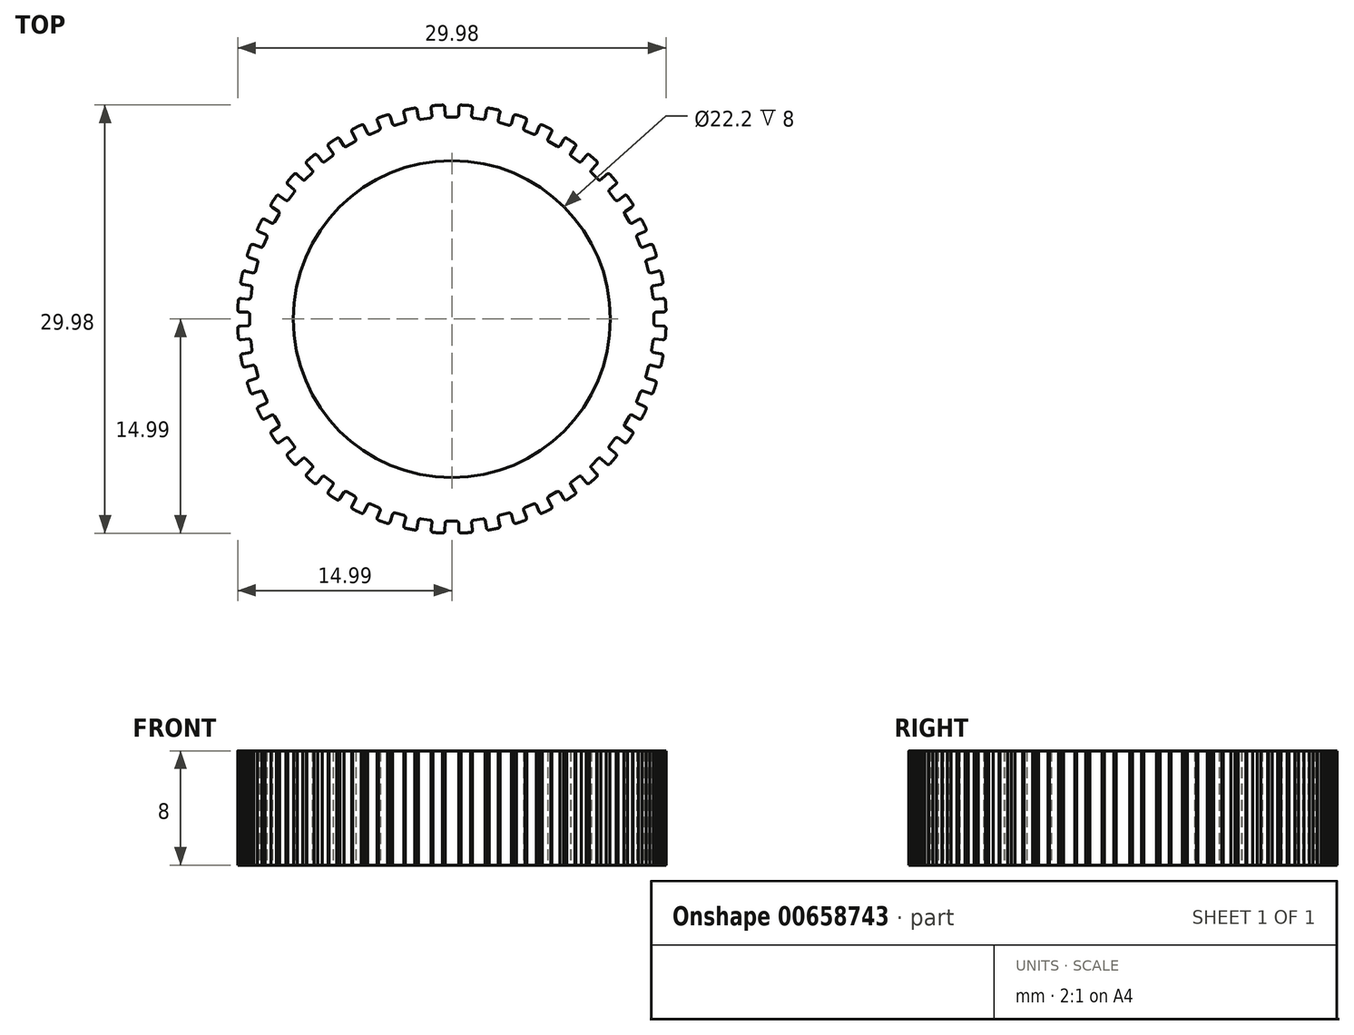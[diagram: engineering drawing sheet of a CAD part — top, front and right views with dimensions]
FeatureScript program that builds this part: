
annotation { "Feature Type Name" : "Feature", "Feature Type Description" : "" }
export const myFeature = defineFeature(function(context is Context, id is Id, definition is map)
    precondition{}
    {
        {
            assignVariable(context, id + "F0", {"name" : "h", "anyValue" : 8});
        }
        {
            var Q0;
            Q0=qCreatedBy(makeId("Top.planeOp"),FACE);
            var sketch = newSketch(context, id + "F1", { "sketchPlane" : qUnion([Q0])});
            skCircle(sketch, "E0", {"center": v(0, 0) * mm, "radius": 15 * mm});
            skCircle(sketch, "E1", {"center": v(0, 0) * mm, "radius": 11.1 * mm});
            skSolve(sketch);
        }
        {
            var Q0;
            Q0=qCreatedBy(makeId("Top.planeOp"),FACE);
            var sketch = newSketch(context, id + "F2", { "sketchPlane" : qUnion([Q0])});
            skCircle(sketch, "E2.0", {"center": v(0, 0) * mm, "radius": 15 * mm});
            skLineSegment(sketch, "E3.top", {"start": v(-0.65, 15.23) * mm, "end": v(0.65, 15.23) * mm});
            skLineSegment(sketch, "E3.left", {"start": v(-0.65, 14.99) * mm, "end": v(-0.65, 15.23) * mm});
            skLineSegment(sketch, "E4", {"start": v(0, 0) * mm, "end": v(-0.5, 15) * mm, "construction": true});
            skArc(sketch, "E5", {"start": v(-0.5, 14.8) * mm, "mid": v(-0.53, 14.93) * mm, "end": v(-0.65, 14.99) * mm});
            skPoint(sketch, "E6", {"position": v(0, 14.15) * mm});
            skLineSegment(sketch, "E7", {"start": v(0, 14.15) * mm, "end": v(-0.32, 14.15) * mm});
            skArc(sketch, "E8", {"start": v(-0.48, 14.27) * mm, "mid": v(-0.42, 14.19) * mm, "end": v(-0.32, 14.15) * mm});
            skArc(sketch, "E9.MirrorCS", {"start": v(0.5, 14.8) * mm, "mid": v(0.53, 14.93) * mm, "end": v(0.65, 14.99) * mm});
            skLineSegment(sketch, "E10", {"start": v(-0.5, 14.8) * mm, "end": v(-0.48, 14.27) * mm});
            skArc(sketch, "E11.MirrorCS", {"start": v(0.48, 14.27) * mm, "mid": v(0.42, 14.19) * mm, "end": v(0.32, 14.15) * mm});
            skLineSegment(sketch, "E12.MirrorCS", {"start": v(0, 0) * mm, "end": v(0.5, 15) * mm, "construction": true});
            skLineSegment(sketch, "E13.MirrorCS", {"start": v(0, 14.15) * mm, "end": v(0.32, 14.15) * mm});
            skLineSegment(sketch, "E14.MirrorCS", {"start": v(0.5, 14.8) * mm, "end": v(0.48, 14.27) * mm});
            skLineSegment(sketch, "E15.MirrorCS", {"start": v(0.65, 14.99) * mm, "end": v(0.65, 15.23) * mm});
            skSolve(sketch);
        }
        {
            var Q0;
            Q0=qCreatedBy(makeId("Top.planeOp"),FACE);
            var sketch = newSketch(context, id + "F3", { "sketchPlane" : qUnion([Q0])});
            skLineSegment(sketch, "E16.0", {"start": v(-0.65, 14.99) * mm, "end": v(-0.65, 15.23) * mm});
            skLineSegment(sketch, "E16.1", {"start": v(0, 14.15) * mm, "end": v(-0.32, 14.15) * mm});
            skLineSegment(sketch, "E16.2", {"start": v(-0.65, 15.23) * mm, "end": v(0.65, 15.23) * mm});
            skLineSegment(sketch, "E16.3", {"start": v(0.65, 14.99) * mm, "end": v(0.65, 15.23) * mm});
            skLineSegment(sketch, "E16.4", {"start": v(0.5, 14.8) * mm, "end": v(0.48, 14.27) * mm});
            skArc(sketch, "E16.5", {"start": v(-0.5, 14.8) * mm, "mid": v(-0.53, 14.93) * mm, "end": v(-0.65, 14.99) * mm});
            skArc(sketch, "E16.6", {"start": v(0.5, 14.8) * mm, "mid": v(0.53, 14.93) * mm, "end": v(0.65, 14.99) * mm});
            skArc(sketch, "E16.7", {"start": v(-0.48, 14.27) * mm, "mid": v(-0.42, 14.19) * mm, "end": v(-0.32, 14.15) * mm});
            skLineSegment(sketch, "E16.8", {"start": v(-0.5, 14.8) * mm, "end": v(-0.48, 14.27) * mm});
            skLineSegment(sketch, "E16.9", {"start": v(0, 14.15) * mm, "end": v(0.32, 14.15) * mm});
            skArc(sketch, "E16.10", {"start": v(0.48, 14.27) * mm, "mid": v(0.42, 14.19) * mm, "end": v(0.32, 14.15) * mm});
            skLineSegment(sketch, "E17.1.0", {"start": v(-1.31, 14.94) * mm, "end": v(-1.34, 15.19) * mm});
            skLineSegment(sketch, "E17.1.1", {"start": v(-1.44, 14.74) * mm, "end": v(-1.4, 14.21) * mm});
            skArc(sketch, "E17.1.2", {"start": v(-2.42, 14.6) * mm, "mid": v(-2.47, 14.73) * mm, "end": v(-2.6, 14.77) * mm});
            skArc(sketch, "E17.1.3", {"start": v(-1.44, 14.74) * mm, "mid": v(-1.42, 14.87) * mm, "end": v(-1.31, 14.94) * mm});
            skArc(sketch, "E17.1.4", {"start": v(-2.34, 14.1) * mm, "mid": v(-2.27, 14) * mm, "end": v(-2.16, 13.99) * mm});
            skLineSegment(sketch, "E17.1.5", {"start": v(-2.42, 14.6) * mm, "end": v(-2.34, 14.1) * mm});
            skLineSegment(sketch, "E17.1.6", {"start": v(-1.85, 14.03) * mm, "end": v(-1.53, 14.07) * mm});
            skArc(sketch, "E17.1.7", {"start": v(-1.4, 14.21) * mm, "mid": v(-1.44, 14.12) * mm, "end": v(-1.53, 14.07) * mm});
            skLineSegment(sketch, "E17.1.8", {"start": v(-2.63, 15.02) * mm, "end": v(-1.34, 15.19) * mm});
            skLineSegment(sketch, "E17.1.9", {"start": v(-1.85, 14.03) * mm, "end": v(-2.16, 13.99) * mm});
            skLineSegment(sketch, "E17.1.10", {"start": v(-2.6, 14.77) * mm, "end": v(-2.63, 15.02) * mm});
            skLineSegment(sketch, "E17.2.0", {"start": v(-3.25, 14.64) * mm, "end": v(-3.31, 14.88) * mm});
            skLineSegment(sketch, "E17.2.1", {"start": v(-3.35, 14.42) * mm, "end": v(-3.23, 13.91) * mm});
            skArc(sketch, "E17.2.2", {"start": v(-4.3, 14.17) * mm, "mid": v(-4.37, 14.28) * mm, "end": v(-4.5, 14.3) * mm});
            skArc(sketch, "E17.2.3", {"start": v(-3.35, 14.42) * mm, "mid": v(-3.35, 14.56) * mm, "end": v(-3.25, 14.64) * mm});
            skArc(sketch, "E17.2.4", {"start": v(-4.15, 13.67) * mm, "mid": v(-4.08, 13.6) * mm, "end": v(-3.97, 13.59) * mm});
            skLineSegment(sketch, "E17.2.5", {"start": v(-4.3, 14.17) * mm, "end": v(-4.15, 13.67) * mm});
            skLineSegment(sketch, "E17.2.6", {"start": v(-3.66, 13.67) * mm, "end": v(-3.35, 13.75) * mm});
            skArc(sketch, "E17.2.7", {"start": v(-3.23, 13.91) * mm, "mid": v(-3.27, 13.81) * mm, "end": v(-3.35, 13.75) * mm});
            skLineSegment(sketch, "E17.2.8", {"start": v(-4.57, 14.55) * mm, "end": v(-3.31, 14.88) * mm});
            skLineSegment(sketch, "E17.2.9", {"start": v(-3.66, 13.67) * mm, "end": v(-3.97, 13.59) * mm});
            skLineSegment(sketch, "E17.2.10", {"start": v(-4.5, 14.3) * mm, "end": v(-4.57, 14.55) * mm});
            skLineSegment(sketch, "E17.3.0", {"start": v(-5.13, 14.1) * mm, "end": v(-5.23, 14.32) * mm});
            skLineSegment(sketch, "E17.3.1", {"start": v(-5.2, 13.86) * mm, "end": v(-5.02, 13.37) * mm});
            skArc(sketch, "E17.3.2", {"start": v(-6.12, 13.48) * mm, "mid": v(-6.2, 13.59) * mm, "end": v(-6.34, 13.6) * mm});
            skArc(sketch, "E17.3.3", {"start": v(-5.2, 13.86) * mm, "mid": v(-5.22, 14) * mm, "end": v(-5.13, 14.1) * mm});
            skArc(sketch, "E17.3.4", {"start": v(-5.9, 13) * mm, "mid": v(-5.82, 12.94) * mm, "end": v(-5.71, 12.95) * mm});
            skLineSegment(sketch, "E17.3.5", {"start": v(-6.12, 13.48) * mm, "end": v(-5.9, 13) * mm});
            skLineSegment(sketch, "E17.3.6", {"start": v(-5.41, 13.07) * mm, "end": v(-5.12, 13.2) * mm});
            skArc(sketch, "E17.3.7", {"start": v(-5.02, 13.37) * mm, "mid": v(-5.04, 13.27) * mm, "end": v(-5.12, 13.2) * mm});
            skLineSegment(sketch, "E17.3.8", {"start": v(-6.43, 13.82) * mm, "end": v(-5.23, 14.32) * mm});
            skLineSegment(sketch, "E17.3.9", {"start": v(-5.41, 13.07) * mm, "end": v(-5.71, 12.95) * mm});
            skLineSegment(sketch, "E17.3.10", {"start": v(-6.34, 13.6) * mm, "end": v(-6.43, 13.82) * mm});
            skLineSegment(sketch, "E17.4.0", {"start": v(-6.93, 13.3) * mm, "end": v(-7.05, 13.52) * mm});
            skLineSegment(sketch, "E17.4.1", {"start": v(-6.97, 13.06) * mm, "end": v(-6.73, 12.6) * mm});
            skArc(sketch, "E17.4.2", {"start": v(-7.83, 12.57) * mm, "mid": v(-7.92, 12.66) * mm, "end": v(-8.06, 12.65) * mm});
            skArc(sketch, "E17.4.3", {"start": v(-6.97, 13.06) * mm, "mid": v(-7, 13.2) * mm, "end": v(-6.93, 13.3) * mm});
            skArc(sketch, "E17.4.4", {"start": v(-7.55, 12.12) * mm, "mid": v(-7.46, 12.07) * mm, "end": v(-7.35, 12.1) * mm});
            skLineSegment(sketch, "E17.4.5", {"start": v(-7.83, 12.57) * mm, "end": v(-7.55, 12.12) * mm});
            skLineSegment(sketch, "E17.4.6", {"start": v(-7.08, 12.25) * mm, "end": v(-6.8, 12.41) * mm});
            skArc(sketch, "E17.4.7", {"start": v(-6.73, 12.6) * mm, "mid": v(-6.73, 12.5) * mm, "end": v(-6.8, 12.41) * mm});
            skLineSegment(sketch, "E17.4.8", {"start": v(-8.18, 12.87) * mm, "end": v(-7.05, 13.52) * mm});
            skLineSegment(sketch, "E17.4.9", {"start": v(-7.08, 12.25) * mm, "end": v(-7.35, 12.1) * mm});
            skLineSegment(sketch, "E17.4.10", {"start": v(-8.06, 12.65) * mm, "end": v(-8.18, 12.87) * mm});
            skLineSegment(sketch, "E17.5.0", {"start": v(-8.6, 12.28) * mm, "end": v(-8.76, 12.48) * mm});
            skLineSegment(sketch, "E17.5.1", {"start": v(-8.62, 12.04) * mm, "end": v(-8.31, 11.61) * mm});
            skArc(sketch, "E17.5.2", {"start": v(-9.4, 11.44) * mm, "mid": v(-9.5, 11.52) * mm, "end": v(-9.64, 11.5) * mm});
            skArc(sketch, "E17.5.3", {"start": v(-8.62, 12.04) * mm, "mid": v(-8.67, 12.17) * mm, "end": v(-8.6, 12.28) * mm});
            skArc(sketch, "E17.5.4", {"start": v(-9.07, 11.04) * mm, "mid": v(-8.97, 11) * mm, "end": v(-8.87, 11.03) * mm});
            skLineSegment(sketch, "E17.5.5", {"start": v(-9.4, 11.44) * mm, "end": v(-9.07, 11.04) * mm});
            skLineSegment(sketch, "E17.5.6", {"start": v(-8.61, 11.23) * mm, "end": v(-8.36, 11.42) * mm});
            skArc(sketch, "E17.5.7", {"start": v(-8.31, 11.61) * mm, "mid": v(-8.3, 11.5) * mm, "end": v(-8.36, 11.42) * mm});
            skLineSegment(sketch, "E17.5.8", {"start": v(-9.79, 11.69) * mm, "end": v(-8.76, 12.48) * mm});
            skLineSegment(sketch, "E17.5.9", {"start": v(-8.61, 11.23) * mm, "end": v(-8.87, 11.03) * mm});
            skLineSegment(sketch, "E17.5.10", {"start": v(-9.64, 11.5) * mm, "end": v(-9.79, 11.69) * mm});
            skLineSegment(sketch, "E17.6.0", {"start": v(-10.14, 11.06) * mm, "end": v(-10.31, 11.23) * mm});
            skLineSegment(sketch, "E17.6.1", {"start": v(-10.12, 10.81) * mm, "end": v(-9.76, 10.43) * mm});
            skArc(sketch, "E17.6.2", {"start": v(-10.81, 10.12) * mm, "mid": v(-10.93, 10.18) * mm, "end": v(-11.06, 10.14) * mm});
            skArc(sketch, "E17.6.3", {"start": v(-10.12, 10.81) * mm, "mid": v(-10.18, 10.93) * mm, "end": v(-10.14, 11.06) * mm});
            skArc(sketch, "E17.6.4", {"start": v(-10.43, 9.76) * mm, "mid": v(-10.33, 9.73) * mm, "end": v(-10.23, 9.78) * mm});
            skLineSegment(sketch, "E17.6.5", {"start": v(-10.81, 10.12) * mm, "end": v(-10.43, 9.76) * mm});
            skLineSegment(sketch, "E17.6.6", {"start": v(-10, 10) * mm, "end": v(-9.78, 10.23) * mm});
            skArc(sketch, "E17.6.7", {"start": v(-9.76, 10.43) * mm, "mid": v(-9.73, 10.33) * mm, "end": v(-9.78, 10.23) * mm});
            skLineSegment(sketch, "E17.6.8", {"start": v(-11.23, 10.31) * mm, "end": v(-10.31, 11.23) * mm});
            skLineSegment(sketch, "E17.6.9", {"start": v(-10, 10) * mm, "end": v(-10.23, 9.78) * mm});
            skLineSegment(sketch, "E17.6.10", {"start": v(-11.06, 10.14) * mm, "end": v(-11.23, 10.31) * mm});
            skLineSegment(sketch, "E17.7.0", {"start": v(-11.5, 9.64) * mm, "end": v(-11.69, 9.79) * mm});
            skLineSegment(sketch, "E17.7.1", {"start": v(-11.44, 9.4) * mm, "end": v(-11.04, 9.07) * mm});
            skArc(sketch, "E17.7.2", {"start": v(-12.04, 8.62) * mm, "mid": v(-12.17, 8.67) * mm, "end": v(-12.28, 8.6) * mm});
            skArc(sketch, "E17.7.3", {"start": v(-11.44, 9.4) * mm, "mid": v(-11.52, 9.5) * mm, "end": v(-11.5, 9.64) * mm});
            skArc(sketch, "E17.7.4", {"start": v(-11.61, 8.31) * mm, "mid": v(-11.5, 8.3) * mm, "end": v(-11.42, 8.36) * mm});
            skLineSegment(sketch, "E17.7.5", {"start": v(-12.04, 8.62) * mm, "end": v(-11.61, 8.31) * mm});
            skLineSegment(sketch, "E17.7.6", {"start": v(-11.23, 8.61) * mm, "end": v(-11.03, 8.87) * mm});
            skArc(sketch, "E17.7.7", {"start": v(-11.04, 9.07) * mm, "mid": v(-11, 8.97) * mm, "end": v(-11.03, 8.87) * mm});
            skLineSegment(sketch, "E17.7.8", {"start": v(-12.48, 8.76) * mm, "end": v(-11.69, 9.79) * mm});
            skLineSegment(sketch, "E17.7.9", {"start": v(-11.23, 8.61) * mm, "end": v(-11.42, 8.36) * mm});
            skLineSegment(sketch, "E17.7.10", {"start": v(-12.28, 8.6) * mm, "end": v(-12.48, 8.76) * mm});
            skLineSegment(sketch, "E17.8.0", {"start": v(-12.65, 8.06) * mm, "end": v(-12.87, 8.18) * mm});
            skLineSegment(sketch, "E17.8.1", {"start": v(-12.57, 7.83) * mm, "end": v(-12.12, 7.55) * mm});
            skArc(sketch, "E17.8.2", {"start": v(-13.06, 6.97) * mm, "mid": v(-13.2, 7) * mm, "end": v(-13.3, 6.93) * mm});
            skArc(sketch, "E17.8.3", {"start": v(-12.57, 7.83) * mm, "mid": v(-12.66, 7.92) * mm, "end": v(-12.65, 8.06) * mm});
            skArc(sketch, "E17.8.4", {"start": v(-12.6, 6.73) * mm, "mid": v(-12.5, 6.73) * mm, "end": v(-12.41, 6.8) * mm});
            skLineSegment(sketch, "E17.8.5", {"start": v(-13.06, 6.97) * mm, "end": v(-12.6, 6.73) * mm});
            skLineSegment(sketch, "E17.8.6", {"start": v(-12.25, 7.08) * mm, "end": v(-12.1, 7.35) * mm});
            skArc(sketch, "E17.8.7", {"start": v(-12.12, 7.55) * mm, "mid": v(-12.07, 7.46) * mm, "end": v(-12.1, 7.35) * mm});
            skLineSegment(sketch, "E17.8.8", {"start": v(-13.52, 7.05) * mm, "end": v(-12.87, 8.18) * mm});
            skLineSegment(sketch, "E17.8.9", {"start": v(-12.25, 7.08) * mm, "end": v(-12.41, 6.8) * mm});
            skLineSegment(sketch, "E17.8.10", {"start": v(-13.3, 6.93) * mm, "end": v(-13.52, 7.05) * mm});
            skLineSegment(sketch, "E17.9.0", {"start": v(-13.6, 6.34) * mm, "end": v(-13.82, 6.43) * mm});
            skLineSegment(sketch, "E17.9.1", {"start": v(-13.48, 6.12) * mm, "end": v(-13, 5.9) * mm});
            skArc(sketch, "E17.9.2", {"start": v(-13.86, 5.2) * mm, "mid": v(-14, 5.22) * mm, "end": v(-14.1, 5.13) * mm});
            skArc(sketch, "E17.9.3", {"start": v(-13.48, 6.12) * mm, "mid": v(-13.59, 6.2) * mm, "end": v(-13.6, 6.34) * mm});
            skArc(sketch, "E17.9.4", {"start": v(-13.37, 5.02) * mm, "mid": v(-13.27, 5.04) * mm, "end": v(-13.2, 5.12) * mm});
            skLineSegment(sketch, "E17.9.5", {"start": v(-13.86, 5.2) * mm, "end": v(-13.37, 5.02) * mm});
            skLineSegment(sketch, "E17.9.6", {"start": v(-13.07, 5.41) * mm, "end": v(-12.95, 5.71) * mm});
            skArc(sketch, "E17.9.7", {"start": v(-13, 5.9) * mm, "mid": v(-12.94, 5.82) * mm, "end": v(-12.95, 5.71) * mm});
            skLineSegment(sketch, "E17.9.8", {"start": v(-14.32, 5.23) * mm, "end": v(-13.82, 6.43) * mm});
            skLineSegment(sketch, "E17.9.9", {"start": v(-13.07, 5.41) * mm, "end": v(-13.2, 5.12) * mm});
            skLineSegment(sketch, "E17.9.10", {"start": v(-14.1, 5.13) * mm, "end": v(-14.32, 5.23) * mm});
            skLineSegment(sketch, "E17.10.0", {"start": v(-14.3, 4.5) * mm, "end": v(-14.55, 4.57) * mm});
            skLineSegment(sketch, "E17.10.1", {"start": v(-14.17, 4.3) * mm, "end": v(-13.67, 4.15) * mm});
            skArc(sketch, "E17.10.2", {"start": v(-14.42, 3.35) * mm, "mid": v(-14.56, 3.35) * mm, "end": v(-14.64, 3.25) * mm});
            skArc(sketch, "E17.10.3", {"start": v(-14.17, 4.3) * mm, "mid": v(-14.28, 4.37) * mm, "end": v(-14.3, 4.5) * mm});
            skArc(sketch, "E17.10.4", {"start": v(-13.91, 3.23) * mm, "mid": v(-13.81, 3.27) * mm, "end": v(-13.75, 3.35) * mm});
            skLineSegment(sketch, "E17.10.5", {"start": v(-14.42, 3.35) * mm, "end": v(-13.91, 3.23) * mm});
            skLineSegment(sketch, "E17.10.6", {"start": v(-13.67, 3.66) * mm, "end": v(-13.59, 3.97) * mm});
            skArc(sketch, "E17.10.7", {"start": v(-13.67, 4.15) * mm, "mid": v(-13.6, 4.08) * mm, "end": v(-13.59, 3.97) * mm});
            skLineSegment(sketch, "E17.10.8", {"start": v(-14.88, 3.31) * mm, "end": v(-14.55, 4.57) * mm});
            skLineSegment(sketch, "E17.10.9", {"start": v(-13.67, 3.66) * mm, "end": v(-13.75, 3.35) * mm});
            skLineSegment(sketch, "E17.10.10", {"start": v(-14.64, 3.25) * mm, "end": v(-14.88, 3.31) * mm});
            skLineSegment(sketch, "E17.11.0", {"start": v(-14.77, 2.6) * mm, "end": v(-15.02, 2.63) * mm});
            skLineSegment(sketch, "E17.11.1", {"start": v(-14.6, 2.42) * mm, "end": v(-14.1, 2.34) * mm});
            skArc(sketch, "E17.11.2", {"start": v(-14.74, 1.44) * mm, "mid": v(-14.87, 1.42) * mm, "end": v(-14.94, 1.31) * mm});
            skArc(sketch, "E17.11.3", {"start": v(-14.6, 2.42) * mm, "mid": v(-14.73, 2.47) * mm, "end": v(-14.77, 2.6) * mm});
            skArc(sketch, "E17.11.4", {"start": v(-14.21, 1.4) * mm, "mid": v(-14.12, 1.44) * mm, "end": v(-14.07, 1.53) * mm});
            skLineSegment(sketch, "E17.11.5", {"start": v(-14.74, 1.44) * mm, "end": v(-14.21, 1.4) * mm});
            skLineSegment(sketch, "E17.11.6", {"start": v(-14.03, 1.85) * mm, "end": v(-13.99, 2.16) * mm});
            skArc(sketch, "E17.11.7", {"start": v(-14.1, 2.34) * mm, "mid": v(-14, 2.27) * mm, "end": v(-13.99, 2.16) * mm});
            skLineSegment(sketch, "E17.11.8", {"start": v(-15.19, 1.34) * mm, "end": v(-15.02, 2.63) * mm});
            skLineSegment(sketch, "E17.11.9", {"start": v(-14.03, 1.85) * mm, "end": v(-14.07, 1.53) * mm});
            skLineSegment(sketch, "E17.11.10", {"start": v(-14.94, 1.31) * mm, "end": v(-15.19, 1.34) * mm});
            skLineSegment(sketch, "E17.12.0", {"start": v(-14.99, 0.65) * mm, "end": v(-15.23, 0.65) * mm});
            skLineSegment(sketch, "E17.12.1", {"start": v(-14.8, 0.5) * mm, "end": v(-14.27, 0.48) * mm});
            skArc(sketch, "E17.12.2", {"start": v(-14.8, -0.5) * mm, "mid": v(-14.93, -0.53) * mm, "end": v(-14.99, -0.65) * mm});
            skArc(sketch, "E17.12.3", {"start": v(-14.8, 0.5) * mm, "mid": v(-14.93, 0.53) * mm, "end": v(-14.99, 0.65) * mm});
            skArc(sketch, "E17.12.4", {"start": v(-14.27, -0.48) * mm, "mid": v(-14.19, -0.42) * mm, "end": v(-14.15, -0.32) * mm});
            skLineSegment(sketch, "E17.12.5", {"start": v(-14.8, -0.5) * mm, "end": v(-14.27, -0.48) * mm});
            skLineSegment(sketch, "E17.12.6", {"start": v(-14.15, 0) * mm, "end": v(-14.15, 0.32) * mm});
            skArc(sketch, "E17.12.7", {"start": v(-14.27, 0.48) * mm, "mid": v(-14.19, 0.42) * mm, "end": v(-14.15, 0.32) * mm});
            skLineSegment(sketch, "E17.12.8", {"start": v(-15.23, -0.65) * mm, "end": v(-15.23, 0.65) * mm});
            skLineSegment(sketch, "E17.12.9", {"start": v(-14.15, 0) * mm, "end": v(-14.15, -0.32) * mm});
            skLineSegment(sketch, "E17.12.10", {"start": v(-14.99, -0.65) * mm, "end": v(-15.23, -0.65) * mm});
            skLineSegment(sketch, "E17.13.0", {"start": v(-14.94, -1.31) * mm, "end": v(-15.19, -1.34) * mm});
            skLineSegment(sketch, "E17.13.1", {"start": v(-14.74, -1.44) * mm, "end": v(-14.21, -1.4) * mm});
            skArc(sketch, "E17.13.2", {"start": v(-14.6, -2.42) * mm, "mid": v(-14.73, -2.47) * mm, "end": v(-14.77, -2.6) * mm});
            skArc(sketch, "E17.13.3", {"start": v(-14.74, -1.44) * mm, "mid": v(-14.87, -1.42) * mm, "end": v(-14.94, -1.31) * mm});
            skArc(sketch, "E17.13.4", {"start": v(-14.1, -2.34) * mm, "mid": v(-14, -2.27) * mm, "end": v(-13.99, -2.16) * mm});
            skLineSegment(sketch, "E17.13.5", {"start": v(-14.6, -2.42) * mm, "end": v(-14.1, -2.34) * mm});
            skLineSegment(sketch, "E17.13.6", {"start": v(-14.03, -1.85) * mm, "end": v(-14.07, -1.53) * mm});
            skArc(sketch, "E17.13.7", {"start": v(-14.21, -1.4) * mm, "mid": v(-14.12, -1.44) * mm, "end": v(-14.07, -1.53) * mm});
            skLineSegment(sketch, "E17.13.8", {"start": v(-15.02, -2.63) * mm, "end": v(-15.19, -1.34) * mm});
            skLineSegment(sketch, "E17.13.9", {"start": v(-14.03, -1.85) * mm, "end": v(-13.99, -2.16) * mm});
            skLineSegment(sketch, "E17.13.10", {"start": v(-14.77, -2.6) * mm, "end": v(-15.02, -2.63) * mm});
            skLineSegment(sketch, "E17.14.0", {"start": v(-14.64, -3.25) * mm, "end": v(-14.88, -3.31) * mm});
            skLineSegment(sketch, "E17.14.1", {"start": v(-14.42, -3.35) * mm, "end": v(-13.91, -3.23) * mm});
            skArc(sketch, "E17.14.2", {"start": v(-14.17, -4.3) * mm, "mid": v(-14.28, -4.37) * mm, "end": v(-14.3, -4.5) * mm});
            skArc(sketch, "E17.14.3", {"start": v(-14.42, -3.35) * mm, "mid": v(-14.56, -3.35) * mm, "end": v(-14.64, -3.25) * mm});
            skArc(sketch, "E17.14.4", {"start": v(-13.67, -4.15) * mm, "mid": v(-13.6, -4.08) * mm, "end": v(-13.59, -3.97) * mm});
            skLineSegment(sketch, "E17.14.5", {"start": v(-14.17, -4.3) * mm, "end": v(-13.67, -4.15) * mm});
            skLineSegment(sketch, "E17.14.6", {"start": v(-13.67, -3.66) * mm, "end": v(-13.75, -3.35) * mm});
            skArc(sketch, "E17.14.7", {"start": v(-13.91, -3.23) * mm, "mid": v(-13.81, -3.27) * mm, "end": v(-13.75, -3.35) * mm});
            skLineSegment(sketch, "E17.14.8", {"start": v(-14.55, -4.57) * mm, "end": v(-14.88, -3.31) * mm});
            skLineSegment(sketch, "E17.14.9", {"start": v(-13.67, -3.66) * mm, "end": v(-13.59, -3.97) * mm});
            skLineSegment(sketch, "E17.14.10", {"start": v(-14.3, -4.5) * mm, "end": v(-14.55, -4.57) * mm});
            skLineSegment(sketch, "E17.15.0", {"start": v(-14.1, -5.13) * mm, "end": v(-14.32, -5.23) * mm});
            skLineSegment(sketch, "E17.15.1", {"start": v(-13.86, -5.2) * mm, "end": v(-13.37, -5.02) * mm});
            skArc(sketch, "E17.15.2", {"start": v(-13.48, -6.12) * mm, "mid": v(-13.59, -6.2) * mm, "end": v(-13.6, -6.34) * mm});
            skArc(sketch, "E17.15.3", {"start": v(-13.86, -5.2) * mm, "mid": v(-14, -5.22) * mm, "end": v(-14.1, -5.13) * mm});
            skArc(sketch, "E17.15.4", {"start": v(-13, -5.9) * mm, "mid": v(-12.94, -5.82) * mm, "end": v(-12.95, -5.71) * mm});
            skLineSegment(sketch, "E17.15.5", {"start": v(-13.48, -6.12) * mm, "end": v(-13, -5.9) * mm});
            skLineSegment(sketch, "E17.15.6", {"start": v(-13.07, -5.41) * mm, "end": v(-13.2, -5.12) * mm});
            skArc(sketch, "E17.15.7", {"start": v(-13.37, -5.02) * mm, "mid": v(-13.27, -5.04) * mm, "end": v(-13.2, -5.12) * mm});
            skLineSegment(sketch, "E17.15.8", {"start": v(-13.82, -6.43) * mm, "end": v(-14.32, -5.23) * mm});
            skLineSegment(sketch, "E17.15.9", {"start": v(-13.07, -5.41) * mm, "end": v(-12.95, -5.71) * mm});
            skLineSegment(sketch, "E17.15.10", {"start": v(-13.6, -6.34) * mm, "end": v(-13.82, -6.43) * mm});
            skLineSegment(sketch, "E17.16.0", {"start": v(-13.3, -6.93) * mm, "end": v(-13.52, -7.05) * mm});
            skLineSegment(sketch, "E17.16.1", {"start": v(-13.06, -6.97) * mm, "end": v(-12.6, -6.73) * mm});
            skArc(sketch, "E17.16.2", {"start": v(-12.57, -7.83) * mm, "mid": v(-12.66, -7.92) * mm, "end": v(-12.65, -8.06) * mm});
            skArc(sketch, "E17.16.3", {"start": v(-13.06, -6.97) * mm, "mid": v(-13.2, -7) * mm, "end": v(-13.3, -6.93) * mm});
            skArc(sketch, "E17.16.4", {"start": v(-12.12, -7.55) * mm, "mid": v(-12.07, -7.46) * mm, "end": v(-12.1, -7.35) * mm});
            skLineSegment(sketch, "E17.16.5", {"start": v(-12.57, -7.83) * mm, "end": v(-12.12, -7.55) * mm});
            skLineSegment(sketch, "E17.16.6", {"start": v(-12.25, -7.07) * mm, "end": v(-12.41, -6.8) * mm});
            skArc(sketch, "E17.16.7", {"start": v(-12.6, -6.73) * mm, "mid": v(-12.5, -6.73) * mm, "end": v(-12.41, -6.8) * mm});
            skLineSegment(sketch, "E17.16.8", {"start": v(-12.87, -8.18) * mm, "end": v(-13.52, -7.05) * mm});
            skLineSegment(sketch, "E17.16.9", {"start": v(-12.25, -7.07) * mm, "end": v(-12.1, -7.35) * mm});
            skLineSegment(sketch, "E17.16.10", {"start": v(-12.65, -8.06) * mm, "end": v(-12.87, -8.18) * mm});
            skLineSegment(sketch, "E17.17.0", {"start": v(-12.28, -8.6) * mm, "end": v(-12.48, -8.76) * mm});
            skLineSegment(sketch, "E17.17.1", {"start": v(-12.04, -8.62) * mm, "end": v(-11.61, -8.31) * mm});
            skArc(sketch, "E17.17.2", {"start": v(-11.44, -9.4) * mm, "mid": v(-11.52, -9.5) * mm, "end": v(-11.5, -9.64) * mm});
            skArc(sketch, "E17.17.3", {"start": v(-12.04, -8.62) * mm, "mid": v(-12.17, -8.67) * mm, "end": v(-12.28, -8.6) * mm});
            skArc(sketch, "E17.17.4", {"start": v(-11.04, -9.07) * mm, "mid": v(-11, -8.97) * mm, "end": v(-11.03, -8.87) * mm});
            skLineSegment(sketch, "E17.17.5", {"start": v(-11.44, -9.4) * mm, "end": v(-11.04, -9.07) * mm});
            skLineSegment(sketch, "E17.17.6", {"start": v(-11.23, -8.61) * mm, "end": v(-11.42, -8.36) * mm});
            skArc(sketch, "E17.17.7", {"start": v(-11.61, -8.31) * mm, "mid": v(-11.5, -8.3) * mm, "end": v(-11.42, -8.36) * mm});
            skLineSegment(sketch, "E17.17.8", {"start": v(-11.69, -9.79) * mm, "end": v(-12.48, -8.76) * mm});
            skLineSegment(sketch, "E17.17.9", {"start": v(-11.23, -8.61) * mm, "end": v(-11.03, -8.87) * mm});
            skLineSegment(sketch, "E17.17.10", {"start": v(-11.5, -9.64) * mm, "end": v(-11.69, -9.79) * mm});
            skLineSegment(sketch, "E17.18.0", {"start": v(-11.06, -10.14) * mm, "end": v(-11.23, -10.31) * mm});
            skLineSegment(sketch, "E17.18.1", {"start": v(-10.81, -10.12) * mm, "end": v(-10.43, -9.76) * mm});
            skArc(sketch, "E17.18.2", {"start": v(-10.12, -10.81) * mm, "mid": v(-10.18, -10.93) * mm, "end": v(-10.14, -11.06) * mm});
            skArc(sketch, "E17.18.3", {"start": v(-10.81, -10.12) * mm, "mid": v(-10.93, -10.18) * mm, "end": v(-11.06, -10.14) * mm});
            skArc(sketch, "E17.18.4", {"start": v(-9.76, -10.43) * mm, "mid": v(-9.73, -10.33) * mm, "end": v(-9.78, -10.23) * mm});
            skLineSegment(sketch, "E17.18.5", {"start": v(-10.12, -10.81) * mm, "end": v(-9.76, -10.43) * mm});
            skLineSegment(sketch, "E17.18.6", {"start": v(-10, -10) * mm, "end": v(-10.23, -9.78) * mm});
            skArc(sketch, "E17.18.7", {"start": v(-10.43, -9.76) * mm, "mid": v(-10.33, -9.73) * mm, "end": v(-10.23, -9.78) * mm});
            skLineSegment(sketch, "E17.18.8", {"start": v(-10.31, -11.23) * mm, "end": v(-11.23, -10.31) * mm});
            skLineSegment(sketch, "E17.18.9", {"start": v(-10, -10) * mm, "end": v(-9.78, -10.23) * mm});
            skLineSegment(sketch, "E17.18.10", {"start": v(-10.14, -11.06) * mm, "end": v(-10.31, -11.23) * mm});
            skLineSegment(sketch, "E17.19.0", {"start": v(-9.64, -11.5) * mm, "end": v(-9.79, -11.69) * mm});
            skLineSegment(sketch, "E17.19.1", {"start": v(-9.4, -11.44) * mm, "end": v(-9.07, -11.04) * mm});
            skArc(sketch, "E17.19.2", {"start": v(-8.62, -12.04) * mm, "mid": v(-8.67, -12.17) * mm, "end": v(-8.6, -12.28) * mm});
            skArc(sketch, "E17.19.3", {"start": v(-9.4, -11.44) * mm, "mid": v(-9.5, -11.52) * mm, "end": v(-9.64, -11.5) * mm});
            skArc(sketch, "E17.19.4", {"start": v(-8.31, -11.61) * mm, "mid": v(-8.3, -11.5) * mm, "end": v(-8.36, -11.42) * mm});
            skLineSegment(sketch, "E17.19.5", {"start": v(-8.62, -12.04) * mm, "end": v(-8.31, -11.61) * mm});
            skLineSegment(sketch, "E17.19.6", {"start": v(-8.61, -11.23) * mm, "end": v(-8.87, -11.03) * mm});
            skArc(sketch, "E17.19.7", {"start": v(-9.07, -11.04) * mm, "mid": v(-8.97, -11) * mm, "end": v(-8.87, -11.03) * mm});
            skLineSegment(sketch, "E17.19.8", {"start": v(-8.76, -12.48) * mm, "end": v(-9.79, -11.69) * mm});
            skLineSegment(sketch, "E17.19.9", {"start": v(-8.61, -11.23) * mm, "end": v(-8.36, -11.42) * mm});
            skLineSegment(sketch, "E17.19.10", {"start": v(-8.6, -12.28) * mm, "end": v(-8.76, -12.48) * mm});
            skLineSegment(sketch, "E17.20.0", {"start": v(-8.06, -12.65) * mm, "end": v(-8.18, -12.87) * mm});
            skLineSegment(sketch, "E17.20.1", {"start": v(-7.83, -12.57) * mm, "end": v(-7.55, -12.12) * mm});
            skArc(sketch, "E17.20.2", {"start": v(-6.97, -13.06) * mm, "mid": v(-7, -13.2) * mm, "end": v(-6.93, -13.3) * mm});
            skArc(sketch, "E17.20.3", {"start": v(-7.83, -12.57) * mm, "mid": v(-7.92, -12.66) * mm, "end": v(-8.06, -12.65) * mm});
            skArc(sketch, "E17.20.4", {"start": v(-6.73, -12.6) * mm, "mid": v(-6.73, -12.5) * mm, "end": v(-6.8, -12.41) * mm});
            skLineSegment(sketch, "E17.20.5", {"start": v(-6.97, -13.06) * mm, "end": v(-6.73, -12.6) * mm});
            skLineSegment(sketch, "E17.20.6", {"start": v(-7.07, -12.25) * mm, "end": v(-7.35, -12.1) * mm});
            skArc(sketch, "E17.20.7", {"start": v(-7.55, -12.12) * mm, "mid": v(-7.46, -12.07) * mm, "end": v(-7.35, -12.1) * mm});
            skLineSegment(sketch, "E17.20.8", {"start": v(-7.05, -13.52) * mm, "end": v(-8.18, -12.87) * mm});
            skLineSegment(sketch, "E17.20.9", {"start": v(-7.07, -12.25) * mm, "end": v(-6.8, -12.41) * mm});
            skLineSegment(sketch, "E17.20.10", {"start": v(-6.93, -13.3) * mm, "end": v(-7.05, -13.52) * mm});
            skLineSegment(sketch, "E17.21.0", {"start": v(-6.34, -13.6) * mm, "end": v(-6.43, -13.82) * mm});
            skLineSegment(sketch, "E17.21.1", {"start": v(-6.12, -13.48) * mm, "end": v(-5.9, -13) * mm});
            skArc(sketch, "E17.21.2", {"start": v(-5.2, -13.86) * mm, "mid": v(-5.22, -14) * mm, "end": v(-5.13, -14.1) * mm});
            skArc(sketch, "E17.21.3", {"start": v(-6.12, -13.48) * mm, "mid": v(-6.2, -13.59) * mm, "end": v(-6.34, -13.6) * mm});
            skArc(sketch, "E17.21.4", {"start": v(-5.02, -13.37) * mm, "mid": v(-5.04, -13.27) * mm, "end": v(-5.12, -13.2) * mm});
            skLineSegment(sketch, "E17.21.5", {"start": v(-5.2, -13.86) * mm, "end": v(-5.02, -13.37) * mm});
            skLineSegment(sketch, "E17.21.6", {"start": v(-5.41, -13.07) * mm, "end": v(-5.71, -12.95) * mm});
            skArc(sketch, "E17.21.7", {"start": v(-5.9, -13) * mm, "mid": v(-5.82, -12.94) * mm, "end": v(-5.71, -12.95) * mm});
            skLineSegment(sketch, "E17.21.8", {"start": v(-5.23, -14.32) * mm, "end": v(-6.43, -13.82) * mm});
            skLineSegment(sketch, "E17.21.9", {"start": v(-5.41, -13.07) * mm, "end": v(-5.12, -13.2) * mm});
            skLineSegment(sketch, "E17.21.10", {"start": v(-5.13, -14.1) * mm, "end": v(-5.23, -14.32) * mm});
            skLineSegment(sketch, "E17.22.0", {"start": v(-4.5, -14.3) * mm, "end": v(-4.57, -14.55) * mm});
            skLineSegment(sketch, "E17.22.1", {"start": v(-4.3, -14.17) * mm, "end": v(-4.15, -13.67) * mm});
            skArc(sketch, "E17.22.2", {"start": v(-3.35, -14.42) * mm, "mid": v(-3.35, -14.56) * mm, "end": v(-3.25, -14.64) * mm});
            skArc(sketch, "E17.22.3", {"start": v(-4.3, -14.17) * mm, "mid": v(-4.37, -14.28) * mm, "end": v(-4.5, -14.3) * mm});
            skArc(sketch, "E17.22.4", {"start": v(-3.23, -13.91) * mm, "mid": v(-3.27, -13.81) * mm, "end": v(-3.35, -13.75) * mm});
            skLineSegment(sketch, "E17.22.5", {"start": v(-3.35, -14.42) * mm, "end": v(-3.23, -13.91) * mm});
            skLineSegment(sketch, "E17.22.6", {"start": v(-3.66, -13.67) * mm, "end": v(-3.97, -13.59) * mm});
            skArc(sketch, "E17.22.7", {"start": v(-4.15, -13.67) * mm, "mid": v(-4.08, -13.6) * mm, "end": v(-3.97, -13.59) * mm});
            skLineSegment(sketch, "E17.22.8", {"start": v(-3.31, -14.88) * mm, "end": v(-4.57, -14.55) * mm});
            skLineSegment(sketch, "E17.22.9", {"start": v(-3.66, -13.67) * mm, "end": v(-3.35, -13.75) * mm});
            skLineSegment(sketch, "E17.22.10", {"start": v(-3.25, -14.64) * mm, "end": v(-3.31, -14.88) * mm});
            skLineSegment(sketch, "E17.23.0", {"start": v(-2.6, -14.77) * mm, "end": v(-2.63, -15.02) * mm});
            skLineSegment(sketch, "E17.23.1", {"start": v(-2.42, -14.6) * mm, "end": v(-2.34, -14.1) * mm});
            skArc(sketch, "E17.23.2", {"start": v(-1.44, -14.74) * mm, "mid": v(-1.42, -14.87) * mm, "end": v(-1.31, -14.94) * mm});
            skArc(sketch, "E17.23.3", {"start": v(-2.42, -14.6) * mm, "mid": v(-2.47, -14.73) * mm, "end": v(-2.6, -14.77) * mm});
            skArc(sketch, "E17.23.4", {"start": v(-1.4, -14.21) * mm, "mid": v(-1.44, -14.12) * mm, "end": v(-1.53, -14.07) * mm});
            skLineSegment(sketch, "E17.23.5", {"start": v(-1.44, -14.74) * mm, "end": v(-1.4, -14.21) * mm});
            skLineSegment(sketch, "E17.23.6", {"start": v(-1.85, -14.03) * mm, "end": v(-2.16, -13.99) * mm});
            skArc(sketch, "E17.23.7", {"start": v(-2.34, -14.1) * mm, "mid": v(-2.27, -14) * mm, "end": v(-2.16, -13.99) * mm});
            skLineSegment(sketch, "E17.23.8", {"start": v(-1.34, -15.19) * mm, "end": v(-2.63, -15.02) * mm});
            skLineSegment(sketch, "E17.23.9", {"start": v(-1.85, -14.03) * mm, "end": v(-1.53, -14.07) * mm});
            skLineSegment(sketch, "E17.23.10", {"start": v(-1.31, -14.94) * mm, "end": v(-1.34, -15.19) * mm});
            skLineSegment(sketch, "E17.24.0", {"start": v(-0.65, -14.99) * mm, "end": v(-0.65, -15.23) * mm});
            skLineSegment(sketch, "E17.24.1", {"start": v(-0.5, -14.8) * mm, "end": v(-0.48, -14.27) * mm});
            skArc(sketch, "E17.24.2", {"start": v(0.5, -14.8) * mm, "mid": v(0.53, -14.93) * mm, "end": v(0.65, -14.99) * mm});
            skArc(sketch, "E17.24.3", {"start": v(-0.5, -14.8) * mm, "mid": v(-0.53, -14.93) * mm, "end": v(-0.65, -14.99) * mm});
            skArc(sketch, "E17.24.4", {"start": v(0.48, -14.27) * mm, "mid": v(0.42, -14.19) * mm, "end": v(0.32, -14.15) * mm});
            skLineSegment(sketch, "E17.24.5", {"start": v(0.5, -14.8) * mm, "end": v(0.48, -14.27) * mm});
            skLineSegment(sketch, "E17.24.6", {"start": v(0, -14.15) * mm, "end": v(-0.32, -14.15) * mm});
            skArc(sketch, "E17.24.7", {"start": v(-0.48, -14.27) * mm, "mid": v(-0.42, -14.19) * mm, "end": v(-0.32, -14.15) * mm});
            skLineSegment(sketch, "E17.24.8", {"start": v(0.65, -15.23) * mm, "end": v(-0.65, -15.23) * mm});
            skLineSegment(sketch, "E17.24.9", {"start": v(0, -14.15) * mm, "end": v(0.32, -14.15) * mm});
            skLineSegment(sketch, "E17.24.10", {"start": v(0.65, -14.99) * mm, "end": v(0.65, -15.23) * mm});
            skLineSegment(sketch, "E17.25.0", {"start": v(1.31, -14.94) * mm, "end": v(1.34, -15.19) * mm});
            skLineSegment(sketch, "E17.25.1", {"start": v(1.44, -14.74) * mm, "end": v(1.4, -14.21) * mm});
            skArc(sketch, "E17.25.2", {"start": v(2.42, -14.6) * mm, "mid": v(2.47, -14.73) * mm, "end": v(2.6, -14.77) * mm});
            skArc(sketch, "E17.25.3", {"start": v(1.44, -14.74) * mm, "mid": v(1.42, -14.87) * mm, "end": v(1.31, -14.94) * mm});
            skArc(sketch, "E17.25.4", {"start": v(2.34, -14.1) * mm, "mid": v(2.27, -14) * mm, "end": v(2.16, -13.99) * mm});
            skLineSegment(sketch, "E17.25.5", {"start": v(2.42, -14.6) * mm, "end": v(2.34, -14.1) * mm});
            skLineSegment(sketch, "E17.25.6", {"start": v(1.85, -14.03) * mm, "end": v(1.53, -14.07) * mm});
            skArc(sketch, "E17.25.7", {"start": v(1.4, -14.21) * mm, "mid": v(1.44, -14.12) * mm, "end": v(1.53, -14.07) * mm});
            skLineSegment(sketch, "E17.25.8", {"start": v(2.63, -15.02) * mm, "end": v(1.34, -15.19) * mm});
            skLineSegment(sketch, "E17.25.9", {"start": v(1.85, -14.03) * mm, "end": v(2.16, -13.99) * mm});
            skLineSegment(sketch, "E17.25.10", {"start": v(2.6, -14.77) * mm, "end": v(2.63, -15.02) * mm});
            skLineSegment(sketch, "E17.26.0", {"start": v(3.25, -14.64) * mm, "end": v(3.31, -14.88) * mm});
            skLineSegment(sketch, "E17.26.1", {"start": v(3.35, -14.42) * mm, "end": v(3.23, -13.91) * mm});
            skArc(sketch, "E17.26.2", {"start": v(4.3, -14.17) * mm, "mid": v(4.37, -14.28) * mm, "end": v(4.5, -14.3) * mm});
            skArc(sketch, "E17.26.3", {"start": v(3.35, -14.42) * mm, "mid": v(3.35, -14.56) * mm, "end": v(3.25, -14.64) * mm});
            skArc(sketch, "E17.26.4", {"start": v(4.15, -13.67) * mm, "mid": v(4.08, -13.6) * mm, "end": v(3.97, -13.59) * mm});
            skLineSegment(sketch, "E17.26.5", {"start": v(4.3, -14.17) * mm, "end": v(4.15, -13.67) * mm});
            skLineSegment(sketch, "E17.26.6", {"start": v(3.66, -13.67) * mm, "end": v(3.35, -13.75) * mm});
            skArc(sketch, "E17.26.7", {"start": v(3.23, -13.91) * mm, "mid": v(3.27, -13.81) * mm, "end": v(3.35, -13.75) * mm});
            skLineSegment(sketch, "E17.26.8", {"start": v(4.57, -14.55) * mm, "end": v(3.31, -14.88) * mm});
            skLineSegment(sketch, "E17.26.9", {"start": v(3.66, -13.67) * mm, "end": v(3.97, -13.59) * mm});
            skLineSegment(sketch, "E17.26.10", {"start": v(4.5, -14.3) * mm, "end": v(4.57, -14.55) * mm});
            skLineSegment(sketch, "E17.27.0", {"start": v(5.13, -14.1) * mm, "end": v(5.23, -14.32) * mm});
            skLineSegment(sketch, "E17.27.1", {"start": v(5.2, -13.86) * mm, "end": v(5.02, -13.37) * mm});
            skArc(sketch, "E17.27.2", {"start": v(6.12, -13.48) * mm, "mid": v(6.2, -13.59) * mm, "end": v(6.34, -13.6) * mm});
            skArc(sketch, "E17.27.3", {"start": v(5.2, -13.86) * mm, "mid": v(5.22, -14) * mm, "end": v(5.13, -14.1) * mm});
            skArc(sketch, "E17.27.4", {"start": v(5.9, -13) * mm, "mid": v(5.82, -12.94) * mm, "end": v(5.71, -12.95) * mm});
            skLineSegment(sketch, "E17.27.5", {"start": v(6.12, -13.48) * mm, "end": v(5.9, -13) * mm});
            skLineSegment(sketch, "E17.27.6", {"start": v(5.41, -13.07) * mm, "end": v(5.12, -13.2) * mm});
            skArc(sketch, "E17.27.7", {"start": v(5.02, -13.37) * mm, "mid": v(5.04, -13.27) * mm, "end": v(5.12, -13.2) * mm});
            skLineSegment(sketch, "E17.27.8", {"start": v(6.43, -13.82) * mm, "end": v(5.23, -14.32) * mm});
            skLineSegment(sketch, "E17.27.9", {"start": v(5.41, -13.07) * mm, "end": v(5.71, -12.95) * mm});
            skLineSegment(sketch, "E17.27.10", {"start": v(6.34, -13.6) * mm, "end": v(6.43, -13.82) * mm});
            skLineSegment(sketch, "E17.28.0", {"start": v(6.93, -13.3) * mm, "end": v(7.05, -13.52) * mm});
            skLineSegment(sketch, "E17.28.1", {"start": v(6.97, -13.06) * mm, "end": v(6.73, -12.6) * mm});
            skArc(sketch, "E17.28.2", {"start": v(7.83, -12.57) * mm, "mid": v(7.92, -12.66) * mm, "end": v(8.06, -12.65) * mm});
            skArc(sketch, "E17.28.3", {"start": v(6.97, -13.06) * mm, "mid": v(7, -13.2) * mm, "end": v(6.93, -13.3) * mm});
            skArc(sketch, "E17.28.4", {"start": v(7.55, -12.12) * mm, "mid": v(7.46, -12.07) * mm, "end": v(7.35, -12.1) * mm});
            skLineSegment(sketch, "E17.28.5", {"start": v(7.83, -12.57) * mm, "end": v(7.55, -12.12) * mm});
            skLineSegment(sketch, "E17.28.6", {"start": v(7.07, -12.25) * mm, "end": v(6.8, -12.41) * mm});
            skArc(sketch, "E17.28.7", {"start": v(6.73, -12.6) * mm, "mid": v(6.73, -12.5) * mm, "end": v(6.8, -12.41) * mm});
            skLineSegment(sketch, "E17.28.8", {"start": v(8.18, -12.87) * mm, "end": v(7.05, -13.52) * mm});
            skLineSegment(sketch, "E17.28.9", {"start": v(7.07, -12.25) * mm, "end": v(7.35, -12.1) * mm});
            skLineSegment(sketch, "E17.28.10", {"start": v(8.06, -12.65) * mm, "end": v(8.18, -12.87) * mm});
            skLineSegment(sketch, "E17.29.0", {"start": v(8.6, -12.28) * mm, "end": v(8.76, -12.48) * mm});
            skLineSegment(sketch, "E17.29.1", {"start": v(8.62, -12.04) * mm, "end": v(8.31, -11.61) * mm});
            skArc(sketch, "E17.29.2", {"start": v(9.4, -11.44) * mm, "mid": v(9.5, -11.52) * mm, "end": v(9.64, -11.5) * mm});
            skArc(sketch, "E17.29.3", {"start": v(8.62, -12.04) * mm, "mid": v(8.67, -12.17) * mm, "end": v(8.6, -12.28) * mm});
            skArc(sketch, "E17.29.4", {"start": v(9.07, -11.04) * mm, "mid": v(8.97, -11) * mm, "end": v(8.87, -11.03) * mm});
            skLineSegment(sketch, "E17.29.5", {"start": v(9.4, -11.44) * mm, "end": v(9.07, -11.04) * mm});
            skLineSegment(sketch, "E17.29.6", {"start": v(8.61, -11.23) * mm, "end": v(8.36, -11.42) * mm});
            skArc(sketch, "E17.29.7", {"start": v(8.31, -11.61) * mm, "mid": v(8.3, -11.5) * mm, "end": v(8.36, -11.42) * mm});
            skLineSegment(sketch, "E17.29.8", {"start": v(9.79, -11.69) * mm, "end": v(8.76, -12.48) * mm});
            skLineSegment(sketch, "E17.29.9", {"start": v(8.61, -11.23) * mm, "end": v(8.87, -11.03) * mm});
            skLineSegment(sketch, "E17.29.10", {"start": v(9.64, -11.5) * mm, "end": v(9.79, -11.69) * mm});
            skLineSegment(sketch, "E17.30.0", {"start": v(10.14, -11.06) * mm, "end": v(10.31, -11.23) * mm});
            skLineSegment(sketch, "E17.30.1", {"start": v(10.12, -10.81) * mm, "end": v(9.76, -10.43) * mm});
            skArc(sketch, "E17.30.2", {"start": v(10.81, -10.12) * mm, "mid": v(10.93, -10.18) * mm, "end": v(11.06, -10.14) * mm});
            skArc(sketch, "E17.30.3", {"start": v(10.12, -10.81) * mm, "mid": v(10.18, -10.93) * mm, "end": v(10.14, -11.06) * mm});
            skArc(sketch, "E17.30.4", {"start": v(10.43, -9.76) * mm, "mid": v(10.33, -9.73) * mm, "end": v(10.23, -9.78) * mm});
            skLineSegment(sketch, "E17.30.5", {"start": v(10.81, -10.12) * mm, "end": v(10.43, -9.76) * mm});
            skLineSegment(sketch, "E17.30.6", {"start": v(10, -10) * mm, "end": v(9.78, -10.23) * mm});
            skArc(sketch, "E17.30.7", {"start": v(9.76, -10.43) * mm, "mid": v(9.73, -10.33) * mm, "end": v(9.78, -10.23) * mm});
            skLineSegment(sketch, "E17.30.8", {"start": v(11.23, -10.31) * mm, "end": v(10.31, -11.23) * mm});
            skLineSegment(sketch, "E17.30.9", {"start": v(10, -10) * mm, "end": v(10.23, -9.78) * mm});
            skLineSegment(sketch, "E17.30.10", {"start": v(11.06, -10.14) * mm, "end": v(11.23, -10.31) * mm});
            skLineSegment(sketch, "E17.31.0", {"start": v(11.5, -9.64) * mm, "end": v(11.69, -9.79) * mm});
            skLineSegment(sketch, "E17.31.1", {"start": v(11.44, -9.4) * mm, "end": v(11.04, -9.07) * mm});
            skArc(sketch, "E17.31.2", {"start": v(12.04, -8.62) * mm, "mid": v(12.17, -8.67) * mm, "end": v(12.28, -8.6) * mm});
            skArc(sketch, "E17.31.3", {"start": v(11.44, -9.4) * mm, "mid": v(11.52, -9.5) * mm, "end": v(11.5, -9.64) * mm});
            skArc(sketch, "E17.31.4", {"start": v(11.61, -8.31) * mm, "mid": v(11.5, -8.3) * mm, "end": v(11.42, -8.36) * mm});
            skLineSegment(sketch, "E17.31.5", {"start": v(12.04, -8.62) * mm, "end": v(11.61, -8.31) * mm});
            skLineSegment(sketch, "E17.31.6", {"start": v(11.23, -8.61) * mm, "end": v(11.03, -8.87) * mm});
            skArc(sketch, "E17.31.7", {"start": v(11.04, -9.07) * mm, "mid": v(11, -8.97) * mm, "end": v(11.03, -8.87) * mm});
            skLineSegment(sketch, "E17.31.8", {"start": v(12.48, -8.76) * mm, "end": v(11.69, -9.79) * mm});
            skLineSegment(sketch, "E17.31.9", {"start": v(11.23, -8.61) * mm, "end": v(11.42, -8.36) * mm});
            skLineSegment(sketch, "E17.31.10", {"start": v(12.28, -8.6) * mm, "end": v(12.48, -8.76) * mm});
            skLineSegment(sketch, "E17.32.0", {"start": v(12.65, -8.06) * mm, "end": v(12.87, -8.18) * mm});
            skLineSegment(sketch, "E17.32.1", {"start": v(12.57, -7.83) * mm, "end": v(12.12, -7.55) * mm});
            skArc(sketch, "E17.32.2", {"start": v(13.06, -6.97) * mm, "mid": v(13.2, -7) * mm, "end": v(13.3, -6.93) * mm});
            skArc(sketch, "E17.32.3", {"start": v(12.57, -7.83) * mm, "mid": v(12.66, -7.92) * mm, "end": v(12.65, -8.06) * mm});
            skArc(sketch, "E17.32.4", {"start": v(12.6, -6.73) * mm, "mid": v(12.5, -6.73) * mm, "end": v(12.41, -6.8) * mm});
            skLineSegment(sketch, "E17.32.5", {"start": v(13.06, -6.97) * mm, "end": v(12.6, -6.73) * mm});
            skLineSegment(sketch, "E17.32.6", {"start": v(12.25, -7.08) * mm, "end": v(12.1, -7.35) * mm});
            skArc(sketch, "E17.32.7", {"start": v(12.12, -7.55) * mm, "mid": v(12.07, -7.46) * mm, "end": v(12.1, -7.35) * mm});
            skLineSegment(sketch, "E17.32.8", {"start": v(13.52, -7.05) * mm, "end": v(12.87, -8.18) * mm});
            skLineSegment(sketch, "E17.32.9", {"start": v(12.25, -7.08) * mm, "end": v(12.41, -6.8) * mm});
            skLineSegment(sketch, "E17.32.10", {"start": v(13.3, -6.93) * mm, "end": v(13.52, -7.05) * mm});
            skLineSegment(sketch, "E17.33.0", {"start": v(13.6, -6.34) * mm, "end": v(13.82, -6.43) * mm});
            skLineSegment(sketch, "E17.33.1", {"start": v(13.48, -6.12) * mm, "end": v(13, -5.9) * mm});
            skArc(sketch, "E17.33.2", {"start": v(13.86, -5.2) * mm, "mid": v(14, -5.22) * mm, "end": v(14.1, -5.13) * mm});
            skArc(sketch, "E17.33.3", {"start": v(13.48, -6.12) * mm, "mid": v(13.59, -6.2) * mm, "end": v(13.6, -6.34) * mm});
            skArc(sketch, "E17.33.4", {"start": v(13.37, -5.02) * mm, "mid": v(13.27, -5.04) * mm, "end": v(13.2, -5.12) * mm});
            skLineSegment(sketch, "E17.33.5", {"start": v(13.86, -5.2) * mm, "end": v(13.37, -5.02) * mm});
            skLineSegment(sketch, "E17.33.6", {"start": v(13.07, -5.41) * mm, "end": v(12.95, -5.71) * mm});
            skArc(sketch, "E17.33.7", {"start": v(13, -5.9) * mm, "mid": v(12.94, -5.82) * mm, "end": v(12.95, -5.71) * mm});
            skLineSegment(sketch, "E17.33.8", {"start": v(14.32, -5.23) * mm, "end": v(13.82, -6.43) * mm});
            skLineSegment(sketch, "E17.33.9", {"start": v(13.07, -5.41) * mm, "end": v(13.2, -5.12) * mm});
            skLineSegment(sketch, "E17.33.10", {"start": v(14.1, -5.13) * mm, "end": v(14.32, -5.23) * mm});
            skLineSegment(sketch, "E17.34.0", {"start": v(14.3, -4.5) * mm, "end": v(14.55, -4.57) * mm});
            skLineSegment(sketch, "E17.34.1", {"start": v(14.17, -4.3) * mm, "end": v(13.67, -4.15) * mm});
            skArc(sketch, "E17.34.2", {"start": v(14.42, -3.35) * mm, "mid": v(14.56, -3.35) * mm, "end": v(14.64, -3.25) * mm});
            skArc(sketch, "E17.34.3", {"start": v(14.17, -4.3) * mm, "mid": v(14.28, -4.37) * mm, "end": v(14.3, -4.5) * mm});
            skArc(sketch, "E17.34.4", {"start": v(13.91, -3.23) * mm, "mid": v(13.81, -3.27) * mm, "end": v(13.75, -3.35) * mm});
            skLineSegment(sketch, "E17.34.5", {"start": v(14.42, -3.35) * mm, "end": v(13.91, -3.23) * mm});
            skLineSegment(sketch, "E17.34.6", {"start": v(13.67, -3.66) * mm, "end": v(13.59, -3.97) * mm});
            skArc(sketch, "E17.34.7", {"start": v(13.67, -4.15) * mm, "mid": v(13.6, -4.08) * mm, "end": v(13.59, -3.97) * mm});
            skLineSegment(sketch, "E17.34.8", {"start": v(14.88, -3.31) * mm, "end": v(14.55, -4.57) * mm});
            skLineSegment(sketch, "E17.34.9", {"start": v(13.67, -3.66) * mm, "end": v(13.75, -3.35) * mm});
            skLineSegment(sketch, "E17.34.10", {"start": v(14.64, -3.25) * mm, "end": v(14.88, -3.31) * mm});
            skLineSegment(sketch, "E17.35.0", {"start": v(14.77, -2.6) * mm, "end": v(15.02, -2.63) * mm});
            skLineSegment(sketch, "E17.35.1", {"start": v(14.6, -2.42) * mm, "end": v(14.1, -2.34) * mm});
            skArc(sketch, "E17.35.2", {"start": v(14.74, -1.44) * mm, "mid": v(14.87, -1.42) * mm, "end": v(14.94, -1.31) * mm});
            skArc(sketch, "E17.35.3", {"start": v(14.6, -2.42) * mm, "mid": v(14.73, -2.47) * mm, "end": v(14.77, -2.6) * mm});
            skArc(sketch, "E17.35.4", {"start": v(14.21, -1.4) * mm, "mid": v(14.12, -1.44) * mm, "end": v(14.07, -1.53) * mm});
            skLineSegment(sketch, "E17.35.5", {"start": v(14.74, -1.44) * mm, "end": v(14.21, -1.4) * mm});
            skLineSegment(sketch, "E17.35.6", {"start": v(14.03, -1.85) * mm, "end": v(13.99, -2.16) * mm});
            skArc(sketch, "E17.35.7", {"start": v(14.1, -2.34) * mm, "mid": v(14, -2.27) * mm, "end": v(13.99, -2.16) * mm});
            skLineSegment(sketch, "E17.35.8", {"start": v(15.19, -1.34) * mm, "end": v(15.02, -2.63) * mm});
            skLineSegment(sketch, "E17.35.9", {"start": v(14.03, -1.85) * mm, "end": v(14.07, -1.53) * mm});
            skLineSegment(sketch, "E17.35.10", {"start": v(14.94, -1.31) * mm, "end": v(15.19, -1.34) * mm});
            skPoint(sketch, "E17.center", {"position": v(0, 0) * mm});
            skLineSegment(sketch, "E18.3.36.0", {"start": v(14.8, -0.5) * mm, "end": v(14.27, -0.48) * mm});
            skArc(sketch, "E18.6.36.0", {"start": v(14.8, 0.5) * mm, "mid": v(14.93, 0.53) * mm, "end": v(14.99, 0.65) * mm});
            skArc(sketch, "E18.10.36.0", {"start": v(14.8, -0.5) * mm, "mid": v(14.93, -0.53) * mm, "end": v(14.99, -0.65) * mm});
            skArc(sketch, "E18.14.36.0", {"start": v(14.27, 0.48) * mm, "mid": v(14.19, 0.42) * mm, "end": v(14.15, 0.32) * mm});
            skLineSegment(sketch, "E18.16.36.0", {"start": v(14.99, -0.65) * mm, "end": v(15.23, -0.65) * mm});
            skLineSegment(sketch, "E18.18.36.0", {"start": v(14.8, 0.5) * mm, "end": v(14.27, 0.48) * mm});
            skLineSegment(sketch, "E18.21.36.0", {"start": v(14.15, 0) * mm, "end": v(14.15, -0.32) * mm});
            skArc(sketch, "E18.24.36.0", {"start": v(14.27, -0.48) * mm, "mid": v(14.19, -0.42) * mm, "end": v(14.15, -0.32) * mm});
            skLineSegment(sketch, "E18.28.36.0", {"start": v(15.23, 0.65) * mm, "end": v(15.23, -0.65) * mm});
            skLineSegment(sketch, "E18.31.36.0", {"start": v(14.15, 0) * mm, "end": v(14.15, 0.32) * mm});
            skLineSegment(sketch, "E18.34.36.0", {"start": v(14.99, 0.65) * mm, "end": v(15.23, 0.65) * mm});
            skLineSegment(sketch, "E18.3.37.0", {"start": v(14.74, 1.44) * mm, "end": v(14.21, 1.4) * mm});
            skArc(sketch, "E18.6.37.0", {"start": v(14.6, 2.42) * mm, "mid": v(14.73, 2.47) * mm, "end": v(14.77, 2.6) * mm});
            skArc(sketch, "E18.10.37.0", {"start": v(14.74, 1.44) * mm, "mid": v(14.87, 1.42) * mm, "end": v(14.94, 1.31) * mm});
            skArc(sketch, "E18.14.37.0", {"start": v(14.1, 2.34) * mm, "mid": v(14, 2.27) * mm, "end": v(13.99, 2.16) * mm});
            skLineSegment(sketch, "E18.16.37.0", {"start": v(14.94, 1.31) * mm, "end": v(15.19, 1.34) * mm});
            skLineSegment(sketch, "E18.18.37.0", {"start": v(14.6, 2.42) * mm, "end": v(14.1, 2.34) * mm});
            skLineSegment(sketch, "E18.21.37.0", {"start": v(14.03, 1.85) * mm, "end": v(14.07, 1.53) * mm});
            skArc(sketch, "E18.24.37.0", {"start": v(14.21, 1.4) * mm, "mid": v(14.12, 1.44) * mm, "end": v(14.07, 1.53) * mm});
            skLineSegment(sketch, "E18.28.37.0", {"start": v(15.02, 2.63) * mm, "end": v(15.19, 1.34) * mm});
            skLineSegment(sketch, "E18.31.37.0", {"start": v(14.03, 1.85) * mm, "end": v(13.99, 2.16) * mm});
            skLineSegment(sketch, "E18.34.37.0", {"start": v(14.77, 2.6) * mm, "end": v(15.02, 2.63) * mm});
            skLineSegment(sketch, "E19.3.38.0", {"start": v(14.42, 3.35) * mm, "end": v(13.91, 3.23) * mm});
            skArc(sketch, "E19.6.38.0", {"start": v(14.17, 4.3) * mm, "mid": v(14.28, 4.37) * mm, "end": v(14.3, 4.5) * mm});
            skArc(sketch, "E19.10.38.0", {"start": v(14.42, 3.35) * mm, "mid": v(14.56, 3.35) * mm, "end": v(14.64, 3.25) * mm});
            skArc(sketch, "E19.14.38.0", {"start": v(13.67, 4.15) * mm, "mid": v(13.6, 4.08) * mm, "end": v(13.59, 3.97) * mm});
            skLineSegment(sketch, "E19.16.38.0", {"start": v(14.64, 3.25) * mm, "end": v(14.88, 3.31) * mm});
            skLineSegment(sketch, "E19.18.38.0", {"start": v(14.17, 4.3) * mm, "end": v(13.67, 4.15) * mm});
            skLineSegment(sketch, "E19.21.38.0", {"start": v(13.67, 3.66) * mm, "end": v(13.75, 3.35) * mm});
            skArc(sketch, "E19.24.38.0", {"start": v(13.91, 3.23) * mm, "mid": v(13.81, 3.27) * mm, "end": v(13.75, 3.35) * mm});
            skLineSegment(sketch, "E19.28.38.0", {"start": v(14.55, 4.57) * mm, "end": v(14.88, 3.31) * mm});
            skLineSegment(sketch, "E19.31.38.0", {"start": v(13.67, 3.66) * mm, "end": v(13.59, 3.97) * mm});
            skLineSegment(sketch, "E19.34.38.0", {"start": v(14.3, 4.5) * mm, "end": v(14.55, 4.57) * mm});
            skLineSegment(sketch, "E19.3.39.0", {"start": v(13.86, 5.2) * mm, "end": v(13.37, 5.02) * mm});
            skArc(sketch, "E19.6.39.0", {"start": v(13.48, 6.12) * mm, "mid": v(13.59, 6.2) * mm, "end": v(13.6, 6.34) * mm});
            skArc(sketch, "E19.10.39.0", {"start": v(13.86, 5.2) * mm, "mid": v(14, 5.22) * mm, "end": v(14.1, 5.13) * mm});
            skArc(sketch, "E19.14.39.0", {"start": v(13, 5.9) * mm, "mid": v(12.94, 5.82) * mm, "end": v(12.95, 5.71) * mm});
            skLineSegment(sketch, "E19.16.39.0", {"start": v(14.1, 5.13) * mm, "end": v(14.32, 5.23) * mm});
            skLineSegment(sketch, "E19.18.39.0", {"start": v(13.48, 6.12) * mm, "end": v(13, 5.9) * mm});
            skLineSegment(sketch, "E19.21.39.0", {"start": v(13.07, 5.41) * mm, "end": v(13.2, 5.12) * mm});
            skArc(sketch, "E19.24.39.0", {"start": v(13.37, 5.02) * mm, "mid": v(13.27, 5.04) * mm, "end": v(13.2, 5.12) * mm});
            skLineSegment(sketch, "E19.28.39.0", {"start": v(13.82, 6.43) * mm, "end": v(14.32, 5.23) * mm});
            skLineSegment(sketch, "E19.31.39.0", {"start": v(13.07, 5.41) * mm, "end": v(12.95, 5.71) * mm});
            skLineSegment(sketch, "E19.34.39.0", {"start": v(13.6, 6.34) * mm, "end": v(13.82, 6.43) * mm});
            skLineSegment(sketch, "E20.3.40.0", {"start": v(13.06, 6.97) * mm, "end": v(12.6, 6.73) * mm});
            skArc(sketch, "E20.6.40.0", {"start": v(12.57, 7.83) * mm, "mid": v(12.66, 7.92) * mm, "end": v(12.65, 8.06) * mm});
            skArc(sketch, "E20.10.40.0", {"start": v(13.06, 6.97) * mm, "mid": v(13.2, 7) * mm, "end": v(13.3, 6.93) * mm});
            skArc(sketch, "E20.14.40.0", {"start": v(12.12, 7.55) * mm, "mid": v(12.07, 7.46) * mm, "end": v(12.1, 7.35) * mm});
            skLineSegment(sketch, "E20.16.40.0", {"start": v(13.3, 6.93) * mm, "end": v(13.52, 7.05) * mm});
            skLineSegment(sketch, "E20.18.40.0", {"start": v(12.57, 7.83) * mm, "end": v(12.12, 7.55) * mm});
            skLineSegment(sketch, "E20.21.40.0", {"start": v(12.25, 7.07) * mm, "end": v(12.41, 6.8) * mm});
            skArc(sketch, "E20.24.40.0", {"start": v(12.6, 6.73) * mm, "mid": v(12.5, 6.73) * mm, "end": v(12.41, 6.8) * mm});
            skLineSegment(sketch, "E20.28.40.0", {"start": v(12.87, 8.18) * mm, "end": v(13.52, 7.05) * mm});
            skLineSegment(sketch, "E20.31.40.0", {"start": v(12.25, 7.08) * mm, "end": v(12.1, 7.35) * mm});
            skLineSegment(sketch, "E20.34.40.0", {"start": v(12.65, 8.06) * mm, "end": v(12.87, 8.18) * mm});
            skLineSegment(sketch, "E20.3.41.0", {"start": v(12.04, 8.62) * mm, "end": v(11.61, 8.31) * mm});
            skArc(sketch, "E20.6.41.0", {"start": v(11.44, 9.4) * mm, "mid": v(11.52, 9.5) * mm, "end": v(11.5, 9.64) * mm});
            skArc(sketch, "E20.10.41.0", {"start": v(12.04, 8.62) * mm, "mid": v(12.17, 8.67) * mm, "end": v(12.28, 8.6) * mm});
            skArc(sketch, "E20.14.41.0", {"start": v(11.04, 9.07) * mm, "mid": v(11, 8.97) * mm, "end": v(11.03, 8.87) * mm});
            skLineSegment(sketch, "E20.16.41.0", {"start": v(12.28, 8.6) * mm, "end": v(12.48, 8.76) * mm});
            skLineSegment(sketch, "E20.18.41.0", {"start": v(11.44, 9.4) * mm, "end": v(11.04, 9.07) * mm});
            skLineSegment(sketch, "E20.21.41.0", {"start": v(11.23, 8.61) * mm, "end": v(11.42, 8.36) * mm});
            skArc(sketch, "E20.24.41.0", {"start": v(11.61, 8.31) * mm, "mid": v(11.5, 8.3) * mm, "end": v(11.42, 8.36) * mm});
            skLineSegment(sketch, "E20.28.41.0", {"start": v(11.69, 9.79) * mm, "end": v(12.48, 8.76) * mm});
            skLineSegment(sketch, "E20.31.41.0", {"start": v(11.23, 8.61) * mm, "end": v(11.03, 8.87) * mm});
            skLineSegment(sketch, "E20.34.41.0", {"start": v(11.5, 9.64) * mm, "end": v(11.69, 9.79) * mm});
            skLineSegment(sketch, "E21.3.42.0", {"start": v(10.81, 10.12) * mm, "end": v(10.43, 9.76) * mm});
            skArc(sketch, "E21.6.42.0", {"start": v(10.12, 10.81) * mm, "mid": v(10.18, 10.93) * mm, "end": v(10.14, 11.06) * mm});
            skArc(sketch, "E21.10.42.0", {"start": v(10.81, 10.12) * mm, "mid": v(10.93, 10.18) * mm, "end": v(11.06, 10.14) * mm});
            skArc(sketch, "E21.14.42.0", {"start": v(9.76, 10.43) * mm, "mid": v(9.73, 10.33) * mm, "end": v(9.78, 10.23) * mm});
            skLineSegment(sketch, "E21.16.42.0", {"start": v(11.06, 10.14) * mm, "end": v(11.23, 10.31) * mm});
            skLineSegment(sketch, "E21.18.42.0", {"start": v(10.12, 10.81) * mm, "end": v(9.76, 10.43) * mm});
            skLineSegment(sketch, "E21.21.42.0", {"start": v(10, 10) * mm, "end": v(10.23, 9.78) * mm});
            skArc(sketch, "E21.24.42.0", {"start": v(10.43, 9.76) * mm, "mid": v(10.33, 9.73) * mm, "end": v(10.23, 9.78) * mm});
            skLineSegment(sketch, "E21.28.42.0", {"start": v(10.31, 11.23) * mm, "end": v(11.23, 10.31) * mm});
            skLineSegment(sketch, "E21.31.42.0", {"start": v(10, 10) * mm, "end": v(9.78, 10.23) * mm});
            skLineSegment(sketch, "E21.34.42.0", {"start": v(10.14, 11.06) * mm, "end": v(10.31, 11.23) * mm});
            skLineSegment(sketch, "E21.3.43.0", {"start": v(9.4, 11.44) * mm, "end": v(9.07, 11.04) * mm});
            skArc(sketch, "E21.6.43.0", {"start": v(8.62, 12.04) * mm, "mid": v(8.67, 12.17) * mm, "end": v(8.6, 12.28) * mm});
            skArc(sketch, "E21.10.43.0", {"start": v(9.4, 11.44) * mm, "mid": v(9.5, 11.52) * mm, "end": v(9.64, 11.5) * mm});
            skArc(sketch, "E21.14.43.0", {"start": v(8.31, 11.61) * mm, "mid": v(8.3, 11.5) * mm, "end": v(8.36, 11.42) * mm});
            skLineSegment(sketch, "E21.16.43.0", {"start": v(9.64, 11.5) * mm, "end": v(9.79, 11.69) * mm});
            skLineSegment(sketch, "E21.18.43.0", {"start": v(8.62, 12.04) * mm, "end": v(8.31, 11.61) * mm});
            skLineSegment(sketch, "E21.21.43.0", {"start": v(8.61, 11.23) * mm, "end": v(8.87, 11.03) * mm});
            skArc(sketch, "E21.24.43.0", {"start": v(9.07, 11.04) * mm, "mid": v(8.97, 11) * mm, "end": v(8.87, 11.03) * mm});
            skLineSegment(sketch, "E21.28.43.0", {"start": v(8.76, 12.48) * mm, "end": v(9.79, 11.69) * mm});
            skLineSegment(sketch, "E21.31.43.0", {"start": v(8.61, 11.23) * mm, "end": v(8.36, 11.42) * mm});
            skLineSegment(sketch, "E21.34.43.0", {"start": v(8.6, 12.28) * mm, "end": v(8.76, 12.48) * mm});
            skLineSegment(sketch, "E21.3.44.0", {"start": v(7.83, 12.57) * mm, "end": v(7.55, 12.12) * mm});
            skArc(sketch, "E21.6.44.0", {"start": v(6.97, 13.06) * mm, "mid": v(7, 13.2) * mm, "end": v(6.93, 13.3) * mm});
            skArc(sketch, "E21.10.44.0", {"start": v(7.83, 12.57) * mm, "mid": v(7.92, 12.66) * mm, "end": v(8.06, 12.65) * mm});
            skArc(sketch, "E21.14.44.0", {"start": v(6.73, 12.6) * mm, "mid": v(6.73, 12.5) * mm, "end": v(6.8, 12.41) * mm});
            skLineSegment(sketch, "E21.16.44.0", {"start": v(8.06, 12.65) * mm, "end": v(8.18, 12.87) * mm});
            skLineSegment(sketch, "E21.18.44.0", {"start": v(6.97, 13.06) * mm, "end": v(6.73, 12.6) * mm});
            skLineSegment(sketch, "E21.21.44.0", {"start": v(7.08, 12.25) * mm, "end": v(7.35, 12.1) * mm});
            skArc(sketch, "E21.24.44.0", {"start": v(7.55, 12.12) * mm, "mid": v(7.46, 12.07) * mm, "end": v(7.35, 12.1) * mm});
            skLineSegment(sketch, "E21.28.44.0", {"start": v(7.05, 13.52) * mm, "end": v(8.18, 12.87) * mm});
            skLineSegment(sketch, "E21.31.44.0", {"start": v(7.08, 12.25) * mm, "end": v(6.8, 12.41) * mm});
            skLineSegment(sketch, "E21.34.44.0", {"start": v(6.93, 13.3) * mm, "end": v(7.05, 13.52) * mm});
            skLineSegment(sketch, "E22.3.45.0", {"start": v(6.12, 13.48) * mm, "end": v(5.9, 13) * mm});
            skArc(sketch, "E22.6.45.0", {"start": v(5.2, 13.86) * mm, "mid": v(5.22, 14) * mm, "end": v(5.13, 14.1) * mm});
            skArc(sketch, "E22.10.45.0", {"start": v(6.12, 13.48) * mm, "mid": v(6.2, 13.59) * mm, "end": v(6.34, 13.6) * mm});
            skArc(sketch, "E22.14.45.0", {"start": v(5.02, 13.37) * mm, "mid": v(5.04, 13.27) * mm, "end": v(5.12, 13.2) * mm});
            skLineSegment(sketch, "E22.16.45.0", {"start": v(6.34, 13.6) * mm, "end": v(6.43, 13.82) * mm});
            skLineSegment(sketch, "E22.18.45.0", {"start": v(5.2, 13.86) * mm, "end": v(5.02, 13.37) * mm});
            skLineSegment(sketch, "E22.21.45.0", {"start": v(5.41, 13.07) * mm, "end": v(5.71, 12.95) * mm});
            skArc(sketch, "E22.24.45.0", {"start": v(5.9, 13) * mm, "mid": v(5.82, 12.94) * mm, "end": v(5.71, 12.95) * mm});
            skLineSegment(sketch, "E22.28.45.0", {"start": v(5.23, 14.32) * mm, "end": v(6.43, 13.82) * mm});
            skLineSegment(sketch, "E22.31.45.0", {"start": v(5.41, 13.07) * mm, "end": v(5.12, 13.2) * mm});
            skLineSegment(sketch, "E22.34.45.0", {"start": v(5.13, 14.1) * mm, "end": v(5.23, 14.32) * mm});
            skLineSegment(sketch, "E22.3.46.0", {"start": v(4.3, 14.17) * mm, "end": v(4.15, 13.67) * mm});
            skArc(sketch, "E22.6.46.0", {"start": v(3.35, 14.42) * mm, "mid": v(3.35, 14.56) * mm, "end": v(3.25, 14.64) * mm});
            skArc(sketch, "E22.10.46.0", {"start": v(4.3, 14.17) * mm, "mid": v(4.37, 14.28) * mm, "end": v(4.5, 14.3) * mm});
            skArc(sketch, "E22.14.46.0", {"start": v(3.23, 13.91) * mm, "mid": v(3.27, 13.81) * mm, "end": v(3.35, 13.75) * mm});
            skLineSegment(sketch, "E22.16.46.0", {"start": v(4.5, 14.3) * mm, "end": v(4.57, 14.55) * mm});
            skLineSegment(sketch, "E22.18.46.0", {"start": v(3.35, 14.42) * mm, "end": v(3.23, 13.91) * mm});
            skLineSegment(sketch, "E22.21.46.0", {"start": v(3.66, 13.67) * mm, "end": v(3.97, 13.59) * mm});
            skArc(sketch, "E22.24.46.0", {"start": v(4.15, 13.67) * mm, "mid": v(4.08, 13.6) * mm, "end": v(3.97, 13.59) * mm});
            skLineSegment(sketch, "E22.28.46.0", {"start": v(3.31, 14.88) * mm, "end": v(4.57, 14.55) * mm});
            skLineSegment(sketch, "E22.31.46.0", {"start": v(3.66, 13.67) * mm, "end": v(3.35, 13.75) * mm});
            skLineSegment(sketch, "E22.34.46.0", {"start": v(3.25, 14.64) * mm, "end": v(3.31, 14.88) * mm});
            skLineSegment(sketch, "E22.3.47.0", {"start": v(2.42, 14.6) * mm, "end": v(2.34, 14.1) * mm});
            skArc(sketch, "E22.6.47.0", {"start": v(1.44, 14.74) * mm, "mid": v(1.42, 14.87) * mm, "end": v(1.31, 14.94) * mm});
            skArc(sketch, "E22.10.47.0", {"start": v(2.42, 14.6) * mm, "mid": v(2.47, 14.73) * mm, "end": v(2.6, 14.77) * mm});
            skArc(sketch, "E22.14.47.0", {"start": v(1.4, 14.21) * mm, "mid": v(1.44, 14.12) * mm, "end": v(1.53, 14.07) * mm});
            skLineSegment(sketch, "E22.16.47.0", {"start": v(2.6, 14.77) * mm, "end": v(2.63, 15.02) * mm});
            skLineSegment(sketch, "E22.18.47.0", {"start": v(1.44, 14.74) * mm, "end": v(1.4, 14.21) * mm});
            skLineSegment(sketch, "E22.21.47.0", {"start": v(1.85, 14.03) * mm, "end": v(2.16, 13.99) * mm});
            skArc(sketch, "E22.24.47.0", {"start": v(2.34, 14.1) * mm, "mid": v(2.27, 14) * mm, "end": v(2.16, 13.99) * mm});
            skLineSegment(sketch, "E22.28.47.0", {"start": v(1.34, 15.19) * mm, "end": v(2.63, 15.02) * mm});
            skLineSegment(sketch, "E22.31.47.0", {"start": v(1.85, 14.03) * mm, "end": v(1.53, 14.07) * mm});
            skLineSegment(sketch, "E22.34.47.0", {"start": v(1.31, 14.94) * mm, "end": v(1.34, 15.19) * mm});
            skSolve(sketch);
        }
        {
            var Q0;
            Q0=makeQuery(id+"F1.imprint","IMPRINT",FACE,{"disambiguationData":[TD([[makeQuery(id+"F1.imprint","IMPRINT",EDGE,{"derivedFrom":sQuery(id+"F1.wireOp",EDGE,"E0")}),1.0]])]});
            extrude(context, id + "F4", {"entities" : qUnion([Q0]), "depth" : (getVariable(context, 'h')) * mm, "offsetDistance" : 25 * mm});
        }
        {
            var Q0;
            Q0=makeQuery(id+"F3.imprint","IMPRINT",FACE,{"disambiguationData":[TD([[makeQuery(id+"F3.imprint","IMPRINT",EDGE,{"derivedFrom":sQuery(id+"F3.wireOp",EDGE,"E17.11.0")}),1.0]])]});
            var Q1;
            Q1=makeQuery(id+"F3.imprint","IMPRINT",FACE,{"disambiguationData":[TD([[makeQuery(id+"F3.imprint","IMPRINT",EDGE,{"derivedFrom":sQuery(id+"F3.wireOp",EDGE,"E17.9.0")}),1.0]])]});
            var Q2;
            Q2=makeQuery(id+"F3.imprint","IMPRINT",FACE,{"disambiguationData":[TD([[makeQuery(id+"F3.imprint","IMPRINT",EDGE,{"derivedFrom":sQuery(id+"F3.wireOp",EDGE,"E17.14.0")}),1.0]])]});
            var Q3;
            Q3=makeQuery(id+"F3.imprint","IMPRINT",FACE,{"disambiguationData":[TD([[makeQuery(id+"F3.imprint","IMPRINT",EDGE,{"derivedFrom":sQuery(id+"F3.wireOp",EDGE,"E17.10.0")}),1.0]])]});
            var Q4;
            Q4=makeQuery(id+"F3.imprint","IMPRINT",FACE,{"disambiguationData":[TD([[makeQuery(id+"F3.imprint","IMPRINT",EDGE,{"derivedFrom":sQuery(id+"F3.wireOp",EDGE,"E17.13.0")}),1.0]])]});
            var Q5;
            Q5=makeQuery(id+"F3.imprint","IMPRINT",FACE,{"disambiguationData":[TD([[makeQuery(id+"F3.imprint","IMPRINT",EDGE,{"derivedFrom":sQuery(id+"F3.wireOp",EDGE,"E17.12.0")}),1.0]])]});
            var Q6;
            Q6=makeQuery(id+"F3.imprint","IMPRINT",FACE,{"disambiguationData":[TD([[makeQuery(id+"F3.imprint","IMPRINT",EDGE,{"derivedFrom":sQuery(id+"F3.wireOp",EDGE,"E17.7.0")}),1.0]])]});
            var Q7;
            Q7=makeQuery(id+"F3.imprint","IMPRINT",FACE,{"disambiguationData":[TD([[makeQuery(id+"F3.imprint","IMPRINT",EDGE,{"derivedFrom":sQuery(id+"F3.wireOp",EDGE,"E17.6.0")}),1.0]])]});
            var Q8;
            Q8=makeQuery(id+"F3.imprint","IMPRINT",FACE,{"disambiguationData":[TD([[makeQuery(id+"F3.imprint","IMPRINT",EDGE,{"derivedFrom":sQuery(id+"F3.wireOp",EDGE,"E17.8.0")}),1.0]])]});
            var Q9;
            Q9=makeQuery(id+"F3.imprint","IMPRINT",FACE,{"disambiguationData":[TD([[makeQuery(id+"F3.imprint","IMPRINT",EDGE,{"derivedFrom":sQuery(id+"F3.wireOp",EDGE,"E17.5.0")}),1.0]])]});
            var Q10;
            Q10=makeQuery(id+"F3.imprint","IMPRINT",FACE,{"disambiguationData":[TD([[makeQuery(id+"F3.imprint","IMPRINT",EDGE,{"derivedFrom":sQuery(id+"F3.wireOp",EDGE,"E17.4.0")}),1.0]])]});
            var Q11;
            Q11=makeQuery(id+"F3.imprint","IMPRINT",FACE,{"disambiguationData":[TD([[makeQuery(id+"F3.imprint","IMPRINT",EDGE,{"derivedFrom":sQuery(id+"F3.wireOp",EDGE,"E17.3.0")}),1.0]])]});
            var Q12;
            Q12=makeQuery(id+"F3.imprint","IMPRINT",FACE,{"disambiguationData":[TD([[makeQuery(id+"F3.imprint","IMPRINT",EDGE,{"derivedFrom":sQuery(id+"F3.wireOp",EDGE,"E17.1.0")}),1.0]])]});
            var Q13;
            Q13=makeQuery(id+"F3.imprint","IMPRINT",FACE,{"disambiguationData":[TD([[makeQuery(id+"F3.imprint","IMPRINT",EDGE,{"derivedFrom":sQuery(id+"F3.wireOp",EDGE,"E17.2.0")}),1.0]])]});
            var Q14;
            Q14=makeQuery(id+"F3.imprint","IMPRINT",FACE,{"disambiguationData":[TD([[makeQuery(id+"F3.imprint","IMPRINT",EDGE,{"derivedFrom":sQuery(id+"F3.wireOp",EDGE,"E21.3.46.0")}),-1.0]])]});
            var Q15;
            Q15=makeQuery(id+"F3.imprint","IMPRINT",FACE,{"disambiguationData":[TD([[makeQuery(id+"F3.imprint","IMPRINT",EDGE,{"derivedFrom":sQuery(id+"F3.wireOp",EDGE,"E21.3.45.0")}),-1.0]])]});
            var Q16;
            Q16=makeQuery(id+"F3.imprint","IMPRINT",FACE,{"disambiguationData":[TD([[makeQuery(id+"F3.imprint","IMPRINT",EDGE,{"derivedFrom":sQuery(id+"F3.wireOp",EDGE,"E21.3.44.0")}),-1.0]])]});
            var Q17;
            Q17=makeQuery(id+"F3.imprint","IMPRINT",FACE,{"disambiguationData":[TD([[makeQuery(id+"F3.imprint","IMPRINT",EDGE,{"derivedFrom":sQuery(id+"F3.wireOp",EDGE,"E21.3.42.0")}),-1.0]])]});
            var Q18;
            Q18=makeQuery(id+"F3.imprint","IMPRINT",FACE,{"disambiguationData":[TD([[makeQuery(id+"F3.imprint","IMPRINT",EDGE,{"derivedFrom":sQuery(id+"F3.wireOp",EDGE,"E20.3.40.0")}),-1.0]])]});
            var Q19;
            Q19=makeQuery(id+"F3.imprint","IMPRINT",FACE,{"disambiguationData":[TD([[makeQuery(id+"F3.imprint","IMPRINT",EDGE,{"derivedFrom":sQuery(id+"F3.wireOp",EDGE,"E21.3.43.0")}),-1.0]])]});
            var Q20;
            Q20=makeQuery(id+"F3.imprint","IMPRINT",FACE,{"disambiguationData":[TD([[makeQuery(id+"F3.imprint","IMPRINT",EDGE,{"derivedFrom":sQuery(id+"F3.wireOp",EDGE,"E19.3.39.0")}),-1.0]])]});
            var Q21;
            Q21=makeQuery(id+"F3.imprint","IMPRINT",FACE,{"disambiguationData":[TD([[makeQuery(id+"F3.imprint","IMPRINT",EDGE,{"derivedFrom":sQuery(id+"F3.wireOp",EDGE,"E20.3.41.0")}),-1.0]])]});
            var Q22;
            Q22=makeQuery(id+"F3.imprint","IMPRINT",FACE,{"disambiguationData":[TD([[makeQuery(id+"F3.imprint","IMPRINT",EDGE,{"derivedFrom":sQuery(id+"F3.wireOp",EDGE,"E19.3.38.0")}),-1.0]])]});
            var Q23;
            Q23=makeQuery(id+"F3.imprint","IMPRINT",FACE,{"disambiguationData":[TD([[makeQuery(id+"F3.imprint","IMPRINT",EDGE,{"derivedFrom":sQuery(id+"F3.wireOp",EDGE,"E17.35.0")}),1.0]])]});
            var Q24;
            Q24=makeQuery(id+"F3.imprint","IMPRINT",FACE,{"disambiguationData":[TD([[makeQuery(id+"F3.imprint","IMPRINT",EDGE,{"derivedFrom":sQuery(id+"F3.wireOp",EDGE,"E18.3.36.0")}),-1.0]])]});
            var Q25;
            Q25=makeQuery(id+"F3.imprint","IMPRINT",FACE,{"disambiguationData":[TD([[makeQuery(id+"F3.imprint","IMPRINT",EDGE,{"derivedFrom":sQuery(id+"F3.wireOp",EDGE,"E18.3.37.0")}),-1.0]])]});
            var Q26;
            Q26=makeQuery(id+"F3.imprint","IMPRINT",FACE,{"disambiguationData":[TD([[makeQuery(id+"F3.imprint","IMPRINT",EDGE,{"derivedFrom":sQuery(id+"F3.wireOp",EDGE,"E17.15.0")}),1.0]])]});
            var Q27;
            Q27=makeQuery(id+"F3.imprint","IMPRINT",FACE,{"disambiguationData":[TD([[makeQuery(id+"F3.imprint","IMPRINT",EDGE,{"derivedFrom":sQuery(id+"F3.wireOp",EDGE,"E17.16.0")}),1.0]])]});
            var Q28;
            Q28=makeQuery(id+"F3.imprint","IMPRINT",FACE,{"disambiguationData":[TD([[makeQuery(id+"F3.imprint","IMPRINT",EDGE,{"derivedFrom":sQuery(id+"F3.wireOp",EDGE,"E17.17.0")}),1.0]])]});
            var Q29;
            Q29=makeQuery(id+"F3.imprint","IMPRINT",FACE,{"disambiguationData":[TD([[makeQuery(id+"F3.imprint","IMPRINT",EDGE,{"derivedFrom":sQuery(id+"F3.wireOp",EDGE,"E17.19.0")}),1.0]])]});
            var Q30;
            Q30=makeQuery(id+"F3.imprint","IMPRINT",FACE,{"disambiguationData":[TD([[makeQuery(id+"F3.imprint","IMPRINT",EDGE,{"derivedFrom":sQuery(id+"F3.wireOp",EDGE,"E17.20.0")}),1.0]])]});
            var Q31;
            Q31=makeQuery(id+"F3.imprint","IMPRINT",FACE,{"disambiguationData":[TD([[makeQuery(id+"F3.imprint","IMPRINT",EDGE,{"derivedFrom":sQuery(id+"F3.wireOp",EDGE,"E17.18.0")}),1.0]])]});
            var Q32;
            Q32=makeQuery(id+"F3.imprint","IMPRINT",FACE,{"disambiguationData":[TD([[makeQuery(id+"F3.imprint","IMPRINT",EDGE,{"derivedFrom":sQuery(id+"F3.wireOp",EDGE,"E17.21.0")}),1.0]])]});
            var Q33;
            Q33=makeQuery(id+"F3.imprint","IMPRINT",FACE,{"disambiguationData":[TD([[makeQuery(id+"F3.imprint","IMPRINT",EDGE,{"derivedFrom":sQuery(id+"F3.wireOp",EDGE,"E17.22.0")}),1.0]])]});
            var Q34;
            Q34=makeQuery(id+"F3.imprint","IMPRINT",FACE,{"disambiguationData":[TD([[makeQuery(id+"F3.imprint","IMPRINT",EDGE,{"derivedFrom":sQuery(id+"F3.wireOp",EDGE,"E17.23.0")}),1.0]])]});
            var Q35;
            Q35=makeQuery(id+"F3.imprint","IMPRINT",FACE,{"disambiguationData":[TD([[makeQuery(id+"F3.imprint","IMPRINT",EDGE,{"derivedFrom":sQuery(id+"F3.wireOp",EDGE,"E17.24.0")}),1.0]])]});
            var Q36;
            Q36=makeQuery(id+"F3.imprint","IMPRINT",FACE,{"disambiguationData":[TD([[makeQuery(id+"F3.imprint","IMPRINT",EDGE,{"derivedFrom":sQuery(id+"F3.wireOp",EDGE,"E17.25.0")}),1.0]])]});
            var Q37;
            Q37=makeQuery(id+"F3.imprint","IMPRINT",FACE,{"disambiguationData":[TD([[makeQuery(id+"F3.imprint","IMPRINT",EDGE,{"derivedFrom":sQuery(id+"F3.wireOp",EDGE,"E17.26.0")}),1.0]])]});
            var Q38;
            Q38=makeQuery(id+"F3.imprint","IMPRINT",FACE,{"disambiguationData":[TD([[makeQuery(id+"F3.imprint","IMPRINT",EDGE,{"derivedFrom":sQuery(id+"F3.wireOp",EDGE,"E17.27.0")}),1.0]])]});
            var Q39;
            Q39=makeQuery(id+"F3.imprint","IMPRINT",FACE,{"disambiguationData":[TD([[makeQuery(id+"F3.imprint","IMPRINT",EDGE,{"derivedFrom":sQuery(id+"F3.wireOp",EDGE,"E17.28.0")}),1.0]])]});
            var Q40;
            Q40=makeQuery(id+"F3.imprint","IMPRINT",FACE,{"disambiguationData":[TD([[makeQuery(id+"F3.imprint","IMPRINT",EDGE,{"derivedFrom":sQuery(id+"F3.wireOp",EDGE,"E17.29.0")}),1.0]])]});
            var Q41;
            Q41=makeQuery(id+"F3.imprint","IMPRINT",FACE,{"disambiguationData":[TD([[makeQuery(id+"F3.imprint","IMPRINT",EDGE,{"derivedFrom":sQuery(id+"F3.wireOp",EDGE,"E17.30.0")}),1.0]])]});
            var Q42;
            Q42=makeQuery(id+"F3.imprint","IMPRINT",FACE,{"disambiguationData":[TD([[makeQuery(id+"F3.imprint","IMPRINT",EDGE,{"derivedFrom":sQuery(id+"F3.wireOp",EDGE,"E17.31.0")}),1.0]])]});
            var Q43;
            Q43=makeQuery(id+"F3.imprint","IMPRINT",FACE,{"disambiguationData":[TD([[makeQuery(id+"F3.imprint","IMPRINT",EDGE,{"derivedFrom":sQuery(id+"F3.wireOp",EDGE,"E17.32.0")}),1.0]])]});
            var Q44;
            Q44=makeQuery(id+"F3.imprint","IMPRINT",FACE,{"disambiguationData":[TD([[makeQuery(id+"F3.imprint","IMPRINT",EDGE,{"derivedFrom":sQuery(id+"F3.wireOp",EDGE,"E17.33.0")}),1.0]])]});
            var Q45;
            Q45=makeQuery(id+"F3.imprint","IMPRINT",FACE,{"disambiguationData":[TD([[makeQuery(id+"F3.imprint","IMPRINT",EDGE,{"derivedFrom":sQuery(id+"F3.wireOp",EDGE,"E17.34.0")}),1.0]])]});
            var Q46;
            Q46=makeQuery(id+"F2.imprint","IMPRINT",FACE,{"disambiguationData":[TD([[makeQuery(id+"F2.imprint","IMPRINT",EDGE,{"derivedFrom":sQuery(id+"F2.wireOp",EDGE,"E3.top")}),-1.0]])]});
            var Q47;
            {var subQ0=sQuery(id+"F2.wireOp",EDGE,"E5");Q47=makeQuery(id+"F2.imprint","IMPRINT",FACE,{"disambiguationData":[TD([[makeQuery(id+"F2.imprint","IMPRINT",EDGE,{"derivedFrom":subQ0}),-1.0]])]});}
            var Q48;
            Q48=makeQuery(id+"F3.imprint","IMPRINT",FACE,{"disambiguationData":[TD([[makeQuery(id+"F3.imprint","IMPRINT",EDGE,{"derivedFrom":sQuery(id+"F3.wireOp",EDGE,"E22.3.48.0")}),-1.0]])]});
            var Q49;
            Q49=makeQuery(id+"F3.imprint","IMPRINT",FACE,{"disambiguationData":[TD([[makeQuery(id+"F3.imprint","IMPRINT",EDGE,{"derivedFrom":sQuery(id+"F3.wireOp",EDGE,"E22.3.47.0")}),-1.0]])]});
            var Q50;
            Q50=makeQuery(id+"F3.imprint","IMPRINT",FACE,{"disambiguationData":[TD([[makeQuery(id+"F3.imprint","IMPRINT",EDGE,{"derivedFrom":sQuery(id+"F3.wireOp",EDGE,"E22.3.46.0")}),-1.0]])]});
            var Q51;
            Q51=makeQuery(id+"F3.imprint","IMPRINT",FACE,{"disambiguationData":[TD([[makeQuery(id+"F3.imprint","IMPRINT",EDGE,{"derivedFrom":sQuery(id+"F3.wireOp",EDGE,"E22.3.45.0")}),-1.0]])]});
            var Q52;
            Q52=makeQuery(id+"F3.imprint","IMPRINT",FACE,{"disambiguationData":[TD([[makeQuery(id+"F3.imprint","IMPRINT",EDGE,{"derivedFrom":sQuery(id+"F3.wireOp",EDGE,"bb1eaab9-c0f5-4631-a9b3-3bb6efd65fb7.3.49.0")}),-1.0]])]});
            extrude(context, id + "F5", {"entities" : qUnion([Q0, Q1, Q2, Q3, Q4, Q5, Q6, Q7, Q8, Q9, Q10, Q11, Q12, Q13, Q14, Q15, Q16, Q17, Q18, Q19, Q20, Q21, Q22, Q23, Q24, Q25, Q26, Q27, Q28, Q29, Q30, Q31, Q32, Q33, Q34, Q35, Q36, Q37, Q38, Q39, Q40, Q41, Q42, Q43, Q44, Q45, Q46, Q47, Q48, Q49, Q50, Q51, Q52]), "operationType" : NewBodyOperationType.REMOVE, "depth" : (getVariable(context, 'h')) * mm, "offsetDistance" : 25 * mm});
        }
    });
